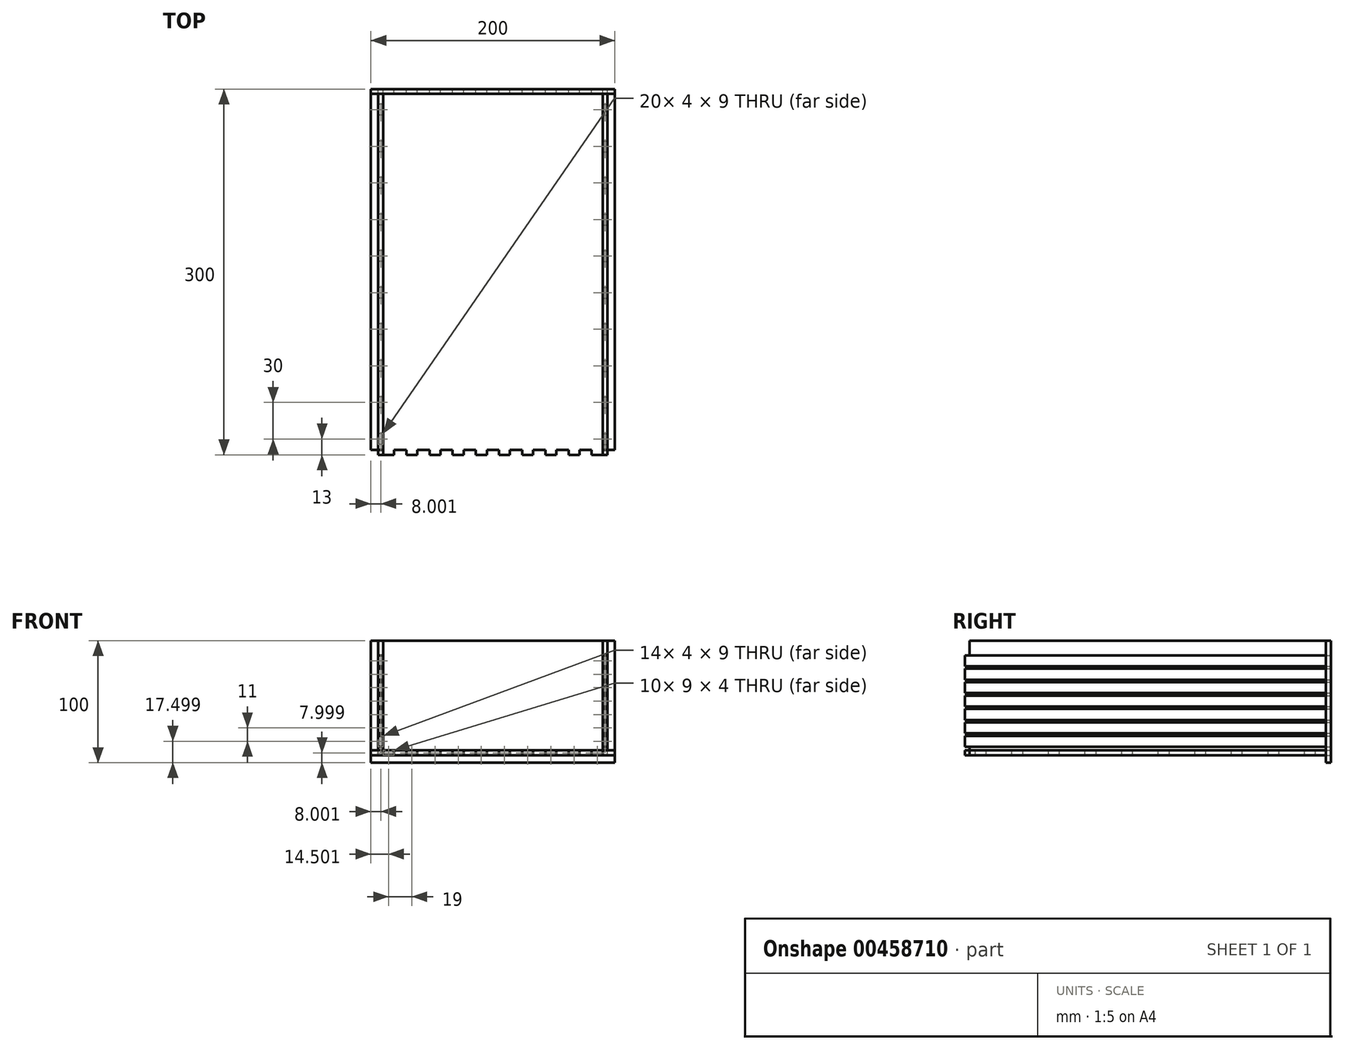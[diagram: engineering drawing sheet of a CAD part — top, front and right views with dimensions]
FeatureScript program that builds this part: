
annotation { "Feature Type Name" : "Feature", "Feature Type Description" : "" }
export const myFeature = defineFeature(function(context is Context, id is Id, definition is map)
    precondition{}
    {
        {
            var Q0;
            Q0=qCreatedBy(makeId("Front.planeOp"),FACE);
            var sketch = newSketch(context, id + "F0", { "sketchPlane" : qUnion([Q0])});
            skLineSegment(sketch, "E0.bottom", {"start": v(-98.88, 5.23) * mm, "end": v(101.12, 5.23) * mm});
            skLineSegment(sketch, "E0.top", {"start": v(-98.88, -94.77) * mm, "end": v(101.12, -94.77) * mm});
            skLineSegment(sketch, "E0.left", {"start": v(-98.88, 5.23) * mm, "end": v(-98.88, -94.77) * mm});
            skLineSegment(sketch, "E0.right", {"start": v(101.12, 5.23) * mm, "end": v(101.12, -94.77) * mm});
            skLineSegment(sketch, "E1.0", {"start": v(-88.88, -4.77) * mm, "end": v(91.12, -4.77) * mm, "construction": true});
            skLineSegment(sketch, "E1.2", {"start": v(-88.88, -84.77) * mm, "end": v(91.12, -84.77) * mm, "construction": true});
            skLineSegment(sketch, "E2.bottom", {"start": v(-88.88, -4.77) * mm, "end": v(-79.88, -4.77) * mm});
            skLineSegment(sketch, "E3.direction1", {"start": v(-88.88, -4.77) * mm, "end": v(-69.88, -4.77) * mm, "construction": true});
            skLineSegment(sketch, "E4.0.9.0", {"start": v(82.12, -4.77) * mm, "end": v(91.12, -4.77) * mm});
            skLineSegment(sketch, "E5", {"start": v(-98.88, -44.77) * mm, "end": v(101.12, -44.77) * mm, "construction": true});
            skLineSegment(sketch, "E6.MirrorCS", {"start": v(-88.88, -84.77) * mm, "end": v(-88.88, -88.77) * mm});
            skLineSegment(sketch, "E7.MirrorCS", {"start": v(-79.88, -84.77) * mm, "end": v(-79.88, -88.77) * mm});
            skLineSegment(sketch, "E8.MirrorCS", {"start": v(-88.88, -88.77) * mm, "end": v(-79.88, -88.77) * mm});
            skLineSegment(sketch, "E9.MirrorCS", {"start": v(-88.88, -84.77) * mm, "end": v(-79.88, -84.77) * mm});
            skLineSegment(sketch, "E10.1.0.0", {"start": v(-60.88, -84.77) * mm, "end": v(-60.88, -88.77) * mm});
            skLineSegment(sketch, "E10.1.0.1", {"start": v(-69.88, -88.77) * mm, "end": v(-60.88, -88.77) * mm});
            skLineSegment(sketch, "E10.1.0.2", {"start": v(-69.88, -84.77) * mm, "end": v(-69.88, -88.77) * mm});
            skLineSegment(sketch, "E10.1.0.3", {"start": v(-69.88, -84.77) * mm, "end": v(-60.88, -84.77) * mm});
            skLineSegment(sketch, "E10.2.0.0", {"start": v(-41.88, -84.77) * mm, "end": v(-41.88, -88.77) * mm});
            skLineSegment(sketch, "E10.2.0.1", {"start": v(-50.88, -88.77) * mm, "end": v(-41.88, -88.77) * mm});
            skLineSegment(sketch, "E10.2.0.2", {"start": v(-50.88, -84.77) * mm, "end": v(-50.88, -88.77) * mm});
            skLineSegment(sketch, "E10.2.0.3", {"start": v(-50.88, -84.77) * mm, "end": v(-41.88, -84.77) * mm});
            skLineSegment(sketch, "E10.3.0.0", {"start": v(-22.88, -84.77) * mm, "end": v(-22.88, -88.77) * mm});
            skLineSegment(sketch, "E10.3.0.1", {"start": v(-31.88, -88.77) * mm, "end": v(-22.88, -88.77) * mm});
            skLineSegment(sketch, "E10.3.0.2", {"start": v(-31.88, -84.77) * mm, "end": v(-31.88, -88.77) * mm});
            skLineSegment(sketch, "E10.3.0.3", {"start": v(-31.88, -84.77) * mm, "end": v(-22.88, -84.77) * mm});
            skLineSegment(sketch, "E10.4.0.0", {"start": v(-3.88, -84.77) * mm, "end": v(-3.88, -88.77) * mm});
            skLineSegment(sketch, "E10.4.0.1", {"start": v(-12.88, -88.77) * mm, "end": v(-3.88, -88.77) * mm});
            skLineSegment(sketch, "E10.4.0.2", {"start": v(-12.88, -84.77) * mm, "end": v(-12.88, -88.77) * mm});
            skLineSegment(sketch, "E10.4.0.3", {"start": v(-12.88, -84.77) * mm, "end": v(-3.88, -84.77) * mm});
            skLineSegment(sketch, "E10.5.0.0", {"start": v(15.12, -84.77) * mm, "end": v(15.12, -88.77) * mm});
            skLineSegment(sketch, "E10.5.0.1", {"start": v(6.12, -88.77) * mm, "end": v(15.12, -88.77) * mm});
            skLineSegment(sketch, "E10.5.0.2", {"start": v(6.12, -84.77) * mm, "end": v(6.12, -88.77) * mm});
            skLineSegment(sketch, "E10.5.0.3", {"start": v(6.12, -84.77) * mm, "end": v(15.12, -84.77) * mm});
            skLineSegment(sketch, "E10.6.0.0", {"start": v(34.12, -84.77) * mm, "end": v(34.12, -88.77) * mm});
            skLineSegment(sketch, "E10.6.0.1", {"start": v(25.12, -88.77) * mm, "end": v(34.12, -88.77) * mm});
            skLineSegment(sketch, "E10.6.0.2", {"start": v(25.12, -84.77) * mm, "end": v(25.12, -88.77) * mm});
            skLineSegment(sketch, "E10.6.0.3", {"start": v(25.12, -84.77) * mm, "end": v(34.12, -84.77) * mm});
            skLineSegment(sketch, "E10.7.0.0", {"start": v(53.12, -84.77) * mm, "end": v(53.12, -88.77) * mm});
            skLineSegment(sketch, "E10.7.0.1", {"start": v(44.12, -88.77) * mm, "end": v(53.12, -88.77) * mm});
            skLineSegment(sketch, "E10.7.0.2", {"start": v(44.12, -84.77) * mm, "end": v(44.12, -88.77) * mm});
            skLineSegment(sketch, "E10.7.0.3", {"start": v(44.12, -84.77) * mm, "end": v(53.12, -84.77) * mm});
            skLineSegment(sketch, "E10.8.0.0", {"start": v(72.12, -84.77) * mm, "end": v(72.12, -88.77) * mm});
            skLineSegment(sketch, "E10.8.0.1", {"start": v(63.12, -88.77) * mm, "end": v(72.12, -88.77) * mm});
            skLineSegment(sketch, "E10.8.0.2", {"start": v(63.12, -84.77) * mm, "end": v(63.12, -88.77) * mm});
            skLineSegment(sketch, "E10.8.0.3", {"start": v(63.12, -84.77) * mm, "end": v(72.12, -84.77) * mm});
            skLineSegment(sketch, "E10.9.0.0", {"start": v(91.12, -84.77) * mm, "end": v(91.12, -88.77) * mm});
            skLineSegment(sketch, "E10.9.0.1", {"start": v(82.12, -88.77) * mm, "end": v(91.12, -88.77) * mm});
            skLineSegment(sketch, "E10.9.0.2", {"start": v(82.12, -84.77) * mm, "end": v(82.12, -88.77) * mm});
            skLineSegment(sketch, "E10.9.0.3", {"start": v(82.12, -84.77) * mm, "end": v(91.12, -84.77) * mm});
            skLineSegment(sketch, "E10.direction1", {"start": v(-79.88, -88.77) * mm, "end": v(-60.88, -88.77) * mm, "construction": true});
            skLineSegment(sketch, "E11.bottom", {"start": v(-88.88, -81.77) * mm, "end": v(-92.88, -81.77) * mm});
            skLineSegment(sketch, "E11.top", {"start": v(-88.88, -72.77) * mm, "end": v(-92.88, -72.77) * mm});
            skLineSegment(sketch, "E11.left", {"start": v(-88.88, -81.77) * mm, "end": v(-88.88, -72.77) * mm});
            skLineSegment(sketch, "E11.right", {"start": v(-92.88, -81.77) * mm, "end": v(-92.88, -72.77) * mm});
            skLineSegment(sketch, "E12.0.1.0", {"start": v(-88.88, -61.77) * mm, "end": v(-92.88, -61.77) * mm});
            skLineSegment(sketch, "E12.0.1.1", {"start": v(-92.88, -70.77) * mm, "end": v(-92.88, -61.77) * mm});
            skLineSegment(sketch, "E12.0.1.2", {"start": v(-88.88, -70.77) * mm, "end": v(-92.88, -70.77) * mm});
            skLineSegment(sketch, "E12.0.1.3", {"start": v(-88.88, -70.77) * mm, "end": v(-88.88, -61.77) * mm});
            skLineSegment(sketch, "E12.0.2.0", {"start": v(-88.88, -50.77) * mm, "end": v(-92.88, -50.77) * mm});
            skLineSegment(sketch, "E12.0.2.1", {"start": v(-92.88, -59.77) * mm, "end": v(-92.88, -50.77) * mm});
            skLineSegment(sketch, "E12.0.2.2", {"start": v(-88.88, -59.77) * mm, "end": v(-92.88, -59.77) * mm});
            skLineSegment(sketch, "E12.0.2.3", {"start": v(-88.88, -59.77) * mm, "end": v(-88.88, -50.77) * mm});
            skLineSegment(sketch, "E12.0.3.0", {"start": v(-88.88, -39.77) * mm, "end": v(-92.88, -39.77) * mm});
            skLineSegment(sketch, "E12.0.3.1", {"start": v(-92.88, -48.77) * mm, "end": v(-92.88, -39.77) * mm});
            skLineSegment(sketch, "E12.0.3.2", {"start": v(-88.88, -48.77) * mm, "end": v(-92.88, -48.77) * mm});
            skLineSegment(sketch, "E12.0.3.3", {"start": v(-88.88, -48.77) * mm, "end": v(-88.88, -39.77) * mm});
            skLineSegment(sketch, "E12.0.4.0", {"start": v(-88.88, -28.77) * mm, "end": v(-92.88, -28.77) * mm});
            skLineSegment(sketch, "E12.0.4.1", {"start": v(-92.88, -37.77) * mm, "end": v(-92.88, -28.77) * mm});
            skLineSegment(sketch, "E12.0.4.2", {"start": v(-88.88, -37.77) * mm, "end": v(-92.88, -37.77) * mm});
            skLineSegment(sketch, "E12.0.4.3", {"start": v(-88.88, -37.77) * mm, "end": v(-88.88, -28.77) * mm});
            skLineSegment(sketch, "E12.0.5.0", {"start": v(-88.88, -17.77) * mm, "end": v(-92.88, -17.77) * mm});
            skLineSegment(sketch, "E12.0.5.1", {"start": v(-92.88, -26.77) * mm, "end": v(-92.88, -17.77) * mm});
            skLineSegment(sketch, "E12.0.5.2", {"start": v(-88.88, -26.77) * mm, "end": v(-92.88, -26.77) * mm});
            skLineSegment(sketch, "E12.0.5.3", {"start": v(-88.88, -26.77) * mm, "end": v(-88.88, -17.77) * mm});
            skLineSegment(sketch, "E12.0.6.0", {"start": v(-88.88, -6.77) * mm, "end": v(-92.88, -6.77) * mm});
            skLineSegment(sketch, "E12.0.6.1", {"start": v(-92.88, -15.77) * mm, "end": v(-92.88, -6.77) * mm});
            skLineSegment(sketch, "E12.0.6.2", {"start": v(-88.88, -15.77) * mm, "end": v(-92.88, -15.77) * mm});
            skLineSegment(sketch, "E12.0.6.3", {"start": v(-88.88, -15.77) * mm, "end": v(-88.88, -6.77) * mm});
            skLineSegment(sketch, "E12.direction1", {"start": v(-92.88, -72.77) * mm, "end": v(-67.88, -72.77) * mm, "construction": true});
            skLineSegment(sketch, "E12.direction2", {"start": v(-92.88, -72.77) * mm, "end": v(-92.88, -61.77) * mm, "construction": true});
            skLineSegment(sketch, "E13", {"start": v(1.12, 5.23) * mm, "end": v(1.12, -94.77) * mm, "construction": true});
            skLineSegment(sketch, "E14.MirrorCS", {"start": v(95.12, -81.77) * mm, "end": v(95.12, -72.77) * mm});
            skLineSegment(sketch, "E15.MirrorCS", {"start": v(91.12, -81.77) * mm, "end": v(95.12, -81.77) * mm});
            skLineSegment(sketch, "E16.MirrorCS", {"start": v(91.12, -81.77) * mm, "end": v(91.12, -72.77) * mm});
            skLineSegment(sketch, "E17.MirrorCS", {"start": v(95.12, -72.77) * mm, "end": v(70.12, -72.77) * mm, "construction": true});
            skLineSegment(sketch, "E18.MirrorCS", {"start": v(91.12, -72.77) * mm, "end": v(95.12, -72.77) * mm});
            skLineSegment(sketch, "E19.0.1.0", {"start": v(91.12, -70.77) * mm, "end": v(91.12, -61.77) * mm});
            skLineSegment(sketch, "E19.0.1.1", {"start": v(91.12, -61.77) * mm, "end": v(95.12, -61.77) * mm});
            skLineSegment(sketch, "E19.0.1.2", {"start": v(95.12, -70.77) * mm, "end": v(95.12, -61.77) * mm});
            skLineSegment(sketch, "E19.0.1.3", {"start": v(91.12, -70.77) * mm, "end": v(95.12, -70.77) * mm});
            skLineSegment(sketch, "E19.0.2.0", {"start": v(91.12, -59.77) * mm, "end": v(91.12, -50.77) * mm});
            skLineSegment(sketch, "E19.0.2.1", {"start": v(91.12, -50.77) * mm, "end": v(95.12, -50.77) * mm});
            skLineSegment(sketch, "E19.0.2.2", {"start": v(95.12, -59.77) * mm, "end": v(95.12, -50.77) * mm});
            skLineSegment(sketch, "E19.0.2.3", {"start": v(91.12, -59.77) * mm, "end": v(95.12, -59.77) * mm});
            skLineSegment(sketch, "E19.0.3.0", {"start": v(91.12, -48.77) * mm, "end": v(91.12, -39.77) * mm});
            skLineSegment(sketch, "E19.0.3.1", {"start": v(91.12, -39.77) * mm, "end": v(95.12, -39.77) * mm});
            skLineSegment(sketch, "E19.0.3.2", {"start": v(95.12, -48.77) * mm, "end": v(95.12, -39.77) * mm});
            skLineSegment(sketch, "E19.0.3.3", {"start": v(91.12, -48.77) * mm, "end": v(95.12, -48.77) * mm});
            skLineSegment(sketch, "E19.0.4.0", {"start": v(91.12, -37.77) * mm, "end": v(91.12, -28.77) * mm});
            skLineSegment(sketch, "E19.0.4.1", {"start": v(91.12, -28.77) * mm, "end": v(95.12, -28.77) * mm});
            skLineSegment(sketch, "E19.0.4.2", {"start": v(95.12, -37.77) * mm, "end": v(95.12, -28.77) * mm});
            skLineSegment(sketch, "E19.0.4.3", {"start": v(91.12, -37.77) * mm, "end": v(95.12, -37.77) * mm});
            skLineSegment(sketch, "E19.0.5.0", {"start": v(91.12, -26.77) * mm, "end": v(91.12, -17.77) * mm});
            skLineSegment(sketch, "E19.0.5.1", {"start": v(91.12, -17.77) * mm, "end": v(95.12, -17.77) * mm});
            skLineSegment(sketch, "E19.0.5.2", {"start": v(95.12, -26.77) * mm, "end": v(95.12, -17.77) * mm});
            skLineSegment(sketch, "E19.0.5.3", {"start": v(91.12, -26.77) * mm, "end": v(95.12, -26.77) * mm});
            skLineSegment(sketch, "E19.0.6.0", {"start": v(91.12, -15.77) * mm, "end": v(91.12, -6.77) * mm});
            skLineSegment(sketch, "E19.0.6.1", {"start": v(91.12, -6.77) * mm, "end": v(95.12, -6.77) * mm});
            skLineSegment(sketch, "E19.0.6.2", {"start": v(95.12, -15.77) * mm, "end": v(95.12, -6.77) * mm});
            skLineSegment(sketch, "E19.0.6.3", {"start": v(91.12, -15.77) * mm, "end": v(95.12, -15.77) * mm});
            skLineSegment(sketch, "E19.direction1", {"start": v(91.12, -81.77) * mm, "end": v(116.12, -81.77) * mm, "construction": true});
            skLineSegment(sketch, "E19.direction2", {"start": v(91.12, -81.77) * mm, "end": v(91.12, -70.77) * mm, "construction": true});
            skLineSegment(sketch, "E20", {"start": v(-84.38, -84.77) * mm, "end": v(-84.38, 5.23) * mm, "construction": true});
            skLineSegment(sketch, "E21.MirrorCS", {"start": v(86.62, -84.77) * mm, "end": v(86.62, 5.23) * mm, "construction": true});
            skSolve(sketch);
        }
        {
            var Q0;
            Q0=makeQuery(id+"F0.imprint","IMPRINT",FACE,{"disambiguationData":[TD([[makeQuery(id+"F0.imprint","IMPRINT",EDGE,{"derivedFrom":sQuery(id+"F0.wireOp",EDGE,"E0.bottom")}),-1.0]])]});
            extrude(context, id + "F1", {"entities" : qUnion([Q0]), "depth" : 4 * mm});
        }
        {
            var Q0;
            Q0=makeQuery(id+"F0.imprint","IMPRINT",FACE,{"disambiguationData":[TD([[makeQuery(id+"F0.imprint","IMPRINT",EDGE,{"derivedFrom":sQuery(id+"F0.wireOp",EDGE,"E10.8.0.0")}),-1.0]])]});
            var Q1;
            Q1=makeQuery(id+"F0.imprint","IMPRINT",FACE,{"disambiguationData":[TD([[makeQuery(id+"F0.imprint","IMPRINT",EDGE,{"derivedFrom":sQuery(id+"F0.wireOp",EDGE,"E10.7.0.0")}),-1.0]])]});
            var Q2;
            Q2=makeQuery(id+"F0.imprint","IMPRINT",FACE,{"disambiguationData":[TD([[makeQuery(id+"F0.imprint","IMPRINT",EDGE,{"derivedFrom":sQuery(id+"F0.wireOp",EDGE,"E10.9.0.0")}),-1.0]])]});
            var Q3;
            Q3=makeQuery(id+"F0.imprint","IMPRINT",FACE,{"disambiguationData":[TD([[makeQuery(id+"F0.imprint","IMPRINT",EDGE,{"derivedFrom":sQuery(id+"F0.wireOp",EDGE,"E10.6.0.0")}),-1.0]])]});
            var Q4;
            Q4=makeQuery(id+"F0.imprint","IMPRINT",FACE,{"disambiguationData":[TD([[makeQuery(id+"F0.imprint","IMPRINT",EDGE,{"derivedFrom":sQuery(id+"F0.wireOp",EDGE,"E10.5.0.0")}),-1.0]])]});
            var Q5;
            Q5=makeQuery(id+"F0.imprint","IMPRINT",FACE,{"disambiguationData":[TD([[makeQuery(id+"F0.imprint","IMPRINT",EDGE,{"derivedFrom":sQuery(id+"F0.wireOp",EDGE,"E10.4.0.0")}),-1.0]])]});
            var Q6;
            Q6=makeQuery(id+"F0.imprint","IMPRINT",FACE,{"disambiguationData":[TD([[makeQuery(id+"F0.imprint","IMPRINT",EDGE,{"derivedFrom":sQuery(id+"F0.wireOp",EDGE,"E10.3.0.0")}),-1.0]])]});
            var Q7;
            Q7=makeQuery(id+"F0.imprint","IMPRINT",FACE,{"disambiguationData":[TD([[makeQuery(id+"F0.imprint","IMPRINT",EDGE,{"derivedFrom":sQuery(id+"F0.wireOp",EDGE,"E10.2.0.0")}),-1.0]])]});
            var Q8;
            Q8=makeQuery(id+"F0.imprint","IMPRINT",FACE,{"disambiguationData":[TD([[makeQuery(id+"F0.imprint","IMPRINT",EDGE,{"derivedFrom":sQuery(id+"F0.wireOp",EDGE,"E10.1.0.0")}),-1.0]])]});
            var Q9;
            Q9=makeQuery(id+"F0.imprint","IMPRINT",FACE,{"disambiguationData":[TD([[makeQuery(id+"F0.imprint","IMPRINT",EDGE,{"derivedFrom":sQuery(id+"F0.wireOp",EDGE,"E6.MirrorCS")}),1.0]])]});
            extrude(context, id + "F2", {"entities" : qUnion([Q0, Q1, Q2, Q3, Q4, Q5, Q6, Q7, Q8, Q9]), "depth" : 300 * mm});
        }
        {
            var Q0;
            Q0=makeQuery(id+"F1.opExtrude","CAP_FACE",FACE,{"disambiguationData":[OSD([sQuery(id+"F0.wireOp",EDGE,"E0.bottom"),sQuery(id+"F0.wireOp",EDGE,"E0.top"),sQuery(id+"F0.wireOp",EDGE,"E0.left"),sQuery(id+"F0.wireOp",EDGE,"E0.right"),sQuery(id+"F0.wireOp",EDGE,"E6.MirrorCS"),sQuery(id+"F0.wireOp",EDGE,"E7.MirrorCS"),sQuery(id+"F0.wireOp",EDGE,"E8.MirrorCS"),sQuery(id+"F0.wireOp",EDGE,"E9.MirrorCS"),sQuery(id+"F0.wireOp",EDGE,"E10.1.0.0"),sQuery(id+"F0.wireOp",EDGE,"E10.1.0.1"),sQuery(id+"F0.wireOp",EDGE,"E10.1.0.2"),sQuery(id+"F0.wireOp",EDGE,"E10.1.0.3"),sQuery(id+"F0.wireOp",EDGE,"E10.2.0.0"),sQuery(id+"F0.wireOp",EDGE,"E10.2.0.1"),sQuery(id+"F0.wireOp",EDGE,"E10.2.0.2"),sQuery(id+"F0.wireOp",EDGE,"E10.2.0.3"),sQuery(id+"F0.wireOp",EDGE,"E10.3.0.0"),sQuery(id+"F0.wireOp",EDGE,"E10.3.0.1"),sQuery(id+"F0.wireOp",EDGE,"E10.3.0.2"),sQuery(id+"F0.wireOp",EDGE,"E10.3.0.3"),sQuery(id+"F0.wireOp",EDGE,"E10.4.0.0"),sQuery(id+"F0.wireOp",EDGE,"E10.4.0.1"),sQuery(id+"F0.wireOp",EDGE,"E10.4.0.2"),sQuery(id+"F0.wireOp",EDGE,"E10.4.0.3"),sQuery(id+"F0.wireOp",EDGE,"E10.5.0.0"),sQuery(id+"F0.wireOp",EDGE,"E10.5.0.1"),sQuery(id+"F0.wireOp",EDGE,"E10.5.0.2"),sQuery(id+"F0.wireOp",EDGE,"E10.5.0.3"),sQuery(id+"F0.wireOp",EDGE,"E10.6.0.0"),sQuery(id+"F0.wireOp",EDGE,"E10.6.0.1"),sQuery(id+"F0.wireOp",EDGE,"E10.6.0.2"),sQuery(id+"F0.wireOp",EDGE,"E10.6.0.3"),sQuery(id+"F0.wireOp",EDGE,"E10.7.0.0"),sQuery(id+"F0.wireOp",EDGE,"E10.7.0.1"),sQuery(id+"F0.wireOp",EDGE,"E10.7.0.2"),sQuery(id+"F0.wireOp",EDGE,"E10.7.0.3"),sQuery(id+"F0.wireOp",EDGE,"E10.8.0.0"),sQuery(id+"F0.wireOp",EDGE,"E10.8.0.1"),sQuery(id+"F0.wireOp",EDGE,"E10.8.0.2"),sQuery(id+"F0.wireOp",EDGE,"E10.8.0.3"),sQuery(id+"F0.wireOp",EDGE,"E10.9.0.0"),sQuery(id+"F0.wireOp",EDGE,"E10.9.0.1"),sQuery(id+"F0.wireOp",EDGE,"E10.9.0.2"),sQuery(id+"F0.wireOp",EDGE,"E10.9.0.3"),sQuery(id+"F0.wireOp",EDGE,"E11.bottom"),sQuery(id+"F0.wireOp",EDGE,"E11.top"),sQuery(id+"F0.wireOp",EDGE,"E11.left"),sQuery(id+"F0.wireOp",EDGE,"E11.right"),sQuery(id+"F0.wireOp",EDGE,"E12.0.1.0"),sQuery(id+"F0.wireOp",EDGE,"E12.0.1.1"),sQuery(id+"F0.wireOp",EDGE,"E12.0.1.2"),sQuery(id+"F0.wireOp",EDGE,"E12.0.1.3"),sQuery(id+"F0.wireOp",EDGE,"E12.0.2.0"),sQuery(id+"F0.wireOp",EDGE,"E12.0.2.1"),sQuery(id+"F0.wireOp",EDGE,"E12.0.2.2"),sQuery(id+"F0.wireOp",EDGE,"E12.0.2.3"),sQuery(id+"F0.wireOp",EDGE,"E12.0.3.0"),sQuery(id+"F0.wireOp",EDGE,"E12.0.3.1"),sQuery(id+"F0.wireOp",EDGE,"E12.0.3.2"),sQuery(id+"F0.wireOp",EDGE,"E12.0.3.3"),sQuery(id+"F0.wireOp",EDGE,"E12.0.4.0"),sQuery(id+"F0.wireOp",EDGE,"E12.0.4.1"),sQuery(id+"F0.wireOp",EDGE,"E12.0.4.2"),sQuery(id+"F0.wireOp",EDGE,"E12.0.4.3"),sQuery(id+"F0.wireOp",EDGE,"E12.0.5.0"),sQuery(id+"F0.wireOp",EDGE,"E12.0.5.1"),sQuery(id+"F0.wireOp",EDGE,"E12.0.5.2"),sQuery(id+"F0.wireOp",EDGE,"E12.0.5.3"),sQuery(id+"F0.wireOp",EDGE,"E12.0.6.0"),sQuery(id+"F0.wireOp",EDGE,"E12.0.6.1"),sQuery(id+"F0.wireOp",EDGE,"E12.0.6.2"),sQuery(id+"F0.wireOp",EDGE,"E12.0.6.3"),sQuery(id+"F0.wireOp",EDGE,"E14.MirrorCS"),sQuery(id+"F0.wireOp",EDGE,"E15.MirrorCS"),sQuery(id+"F0.wireOp",EDGE,"E16.MirrorCS"),sQuery(id+"F0.wireOp",EDGE,"E18.MirrorCS"),sQuery(id+"F0.wireOp",EDGE,"E19.0.1.0"),sQuery(id+"F0.wireOp",EDGE,"E19.0.1.1"),sQuery(id+"F0.wireOp",EDGE,"E19.0.1.2"),sQuery(id+"F0.wireOp",EDGE,"E19.0.1.3"),sQuery(id+"F0.wireOp",EDGE,"E19.0.2.0"),sQuery(id+"F0.wireOp",EDGE,"E19.0.2.1"),sQuery(id+"F0.wireOp",EDGE,"E19.0.2.2"),sQuery(id+"F0.wireOp",EDGE,"E19.0.2.3"),sQuery(id+"F0.wireOp",EDGE,"E19.0.3.0"),sQuery(id+"F0.wireOp",EDGE,"E19.0.3.1"),sQuery(id+"F0.wireOp",EDGE,"E19.0.3.2"),sQuery(id+"F0.wireOp",EDGE,"E19.0.3.3"),sQuery(id+"F0.wireOp",EDGE,"E19.0.4.0"),sQuery(id+"F0.wireOp",EDGE,"E19.0.4.1"),sQuery(id+"F0.wireOp",EDGE,"E19.0.4.2"),sQuery(id+"F0.wireOp",EDGE,"E19.0.4.3"),sQuery(id+"F0.wireOp",EDGE,"E19.0.5.0"),sQuery(id+"F0.wireOp",EDGE,"E19.0.5.1"),sQuery(id+"F0.wireOp",EDGE,"E19.0.5.2"),sQuery(id+"F0.wireOp",EDGE,"E19.0.5.3"),sQuery(id+"F0.wireOp",EDGE,"E19.0.6.0"),sQuery(id+"F0.wireOp",EDGE,"E19.0.6.1"),sQuery(id+"F0.wireOp",EDGE,"E19.0.6.2"),sQuery(id+"F0.wireOp",EDGE,"E19.0.6.3")])],"isStart":false});
            var sketch = newSketch(context, id + "F3", { "sketchPlane" : qUnion([Q0])});
            skLineSegment(sketch, "E22.bottom", {"start": v(-79.88, -84.77) * mm, "end": v(-69.88, -84.77) * mm});
            skLineSegment(sketch, "E22.top", {"start": v(-79.88, -88.77) * mm, "end": v(-69.88, -88.77) * mm});
            skLineSegment(sketch, "E22.left", {"start": v(-79.88, -84.77) * mm, "end": v(-79.88, -88.77) * mm});
            skLineSegment(sketch, "E22.right", {"start": v(-69.88, -84.77) * mm, "end": v(-69.88, -88.77) * mm});
            skLineSegment(sketch, "E23.1.0.0", {"start": v(-60.88, -84.77) * mm, "end": v(-50.88, -84.77) * mm});
            skLineSegment(sketch, "E23.1.0.1", {"start": v(-60.88, -84.77) * mm, "end": v(-60.88, -88.77) * mm});
            skLineSegment(sketch, "E23.1.0.2", {"start": v(-60.88, -88.77) * mm, "end": v(-50.88, -88.77) * mm});
            skLineSegment(sketch, "E23.1.0.3", {"start": v(-50.88, -84.77) * mm, "end": v(-50.88, -88.77) * mm});
            skLineSegment(sketch, "E23.2.0.0", {"start": v(-41.88, -84.77) * mm, "end": v(-31.88, -84.77) * mm});
            skLineSegment(sketch, "E23.2.0.1", {"start": v(-41.88, -84.77) * mm, "end": v(-41.88, -88.77) * mm});
            skLineSegment(sketch, "E23.2.0.2", {"start": v(-41.88, -88.77) * mm, "end": v(-31.88, -88.77) * mm});
            skLineSegment(sketch, "E23.2.0.3", {"start": v(-31.88, -84.77) * mm, "end": v(-31.88, -88.77) * mm});
            skLineSegment(sketch, "E23.3.0.0", {"start": v(-22.88, -84.77) * mm, "end": v(-12.88, -84.77) * mm});
            skLineSegment(sketch, "E23.3.0.1", {"start": v(-22.88, -84.77) * mm, "end": v(-22.88, -88.77) * mm});
            skLineSegment(sketch, "E23.3.0.2", {"start": v(-22.88, -88.77) * mm, "end": v(-12.88, -88.77) * mm});
            skLineSegment(sketch, "E23.3.0.3", {"start": v(-12.88, -84.77) * mm, "end": v(-12.88, -88.77) * mm});
            skLineSegment(sketch, "E23.4.0.0", {"start": v(-3.88, -84.77) * mm, "end": v(6.12, -84.77) * mm});
            skLineSegment(sketch, "E23.4.0.1", {"start": v(-3.88, -84.77) * mm, "end": v(-3.88, -88.77) * mm});
            skLineSegment(sketch, "E23.4.0.2", {"start": v(-3.88, -88.77) * mm, "end": v(6.12, -88.77) * mm});
            skLineSegment(sketch, "E23.4.0.3", {"start": v(6.12, -84.77) * mm, "end": v(6.12, -88.77) * mm});
            skLineSegment(sketch, "E23.5.0.0", {"start": v(15.12, -84.77) * mm, "end": v(25.12, -84.77) * mm});
            skLineSegment(sketch, "E23.5.0.1", {"start": v(15.12, -84.77) * mm, "end": v(15.12, -88.77) * mm});
            skLineSegment(sketch, "E23.5.0.2", {"start": v(15.12, -88.77) * mm, "end": v(25.12, -88.77) * mm});
            skLineSegment(sketch, "E23.5.0.3", {"start": v(25.12, -84.77) * mm, "end": v(25.12, -88.77) * mm});
            skLineSegment(sketch, "E23.6.0.0", {"start": v(34.12, -84.77) * mm, "end": v(44.12, -84.77) * mm});
            skLineSegment(sketch, "E23.6.0.1", {"start": v(34.12, -84.77) * mm, "end": v(34.12, -88.77) * mm});
            skLineSegment(sketch, "E23.6.0.2", {"start": v(34.12, -88.77) * mm, "end": v(44.12, -88.77) * mm});
            skLineSegment(sketch, "E23.6.0.3", {"start": v(44.12, -84.77) * mm, "end": v(44.12, -88.77) * mm});
            skLineSegment(sketch, "E23.7.0.0", {"start": v(53.12, -84.77) * mm, "end": v(63.12, -84.77) * mm});
            skLineSegment(sketch, "E23.7.0.1", {"start": v(53.12, -84.77) * mm, "end": v(53.12, -88.77) * mm});
            skLineSegment(sketch, "E23.7.0.2", {"start": v(53.12, -88.77) * mm, "end": v(63.12, -88.77) * mm});
            skLineSegment(sketch, "E23.7.0.3", {"start": v(63.12, -84.77) * mm, "end": v(63.12, -88.77) * mm});
            skLineSegment(sketch, "E23.8.0.0", {"start": v(72.12, -84.77) * mm, "end": v(82.12, -84.77) * mm});
            skLineSegment(sketch, "E23.8.0.1", {"start": v(72.12, -84.77) * mm, "end": v(72.12, -88.77) * mm});
            skLineSegment(sketch, "E23.8.0.2", {"start": v(72.12, -88.77) * mm, "end": v(82.12, -88.77) * mm});
            skLineSegment(sketch, "E23.8.0.3", {"start": v(82.12, -84.77) * mm, "end": v(82.12, -88.77) * mm});
            skLineSegment(sketch, "E23.direction1", {"start": v(-79.88, -84.77) * mm, "end": v(-60.88, -84.77) * mm, "construction": true});
            skSolve(sketch);
        }
        {
            var Q0;
            Q0=makeQuery(id+"F3.imprint","IMPRINT",FACE,{"disambiguationData":[TD([[makeQuery(id+"F3.imprint","IMPRINT",EDGE,{"derivedFrom":sQuery(id+"F3.wireOp",EDGE,"E22.bottom")}),-1.0]])]});
            var Q1;
            Q1=makeQuery(id+"F3.imprint","IMPRINT",FACE,{"disambiguationData":[TD([[makeQuery(id+"F3.imprint","IMPRINT",EDGE,{"derivedFrom":sQuery(id+"F3.wireOp",EDGE,"E23.1.0.0")}),-1.0]])]});
            var Q2;
            Q2=makeQuery(id+"F3.imprint","IMPRINT",FACE,{"disambiguationData":[TD([[makeQuery(id+"F3.imprint","IMPRINT",EDGE,{"derivedFrom":sQuery(id+"F3.wireOp",EDGE,"E23.2.0.0")}),-1.0]])]});
            var Q3;
            Q3=makeQuery(id+"F3.imprint","IMPRINT",FACE,{"disambiguationData":[TD([[makeQuery(id+"F3.imprint","IMPRINT",EDGE,{"derivedFrom":sQuery(id+"F3.wireOp",EDGE,"E23.3.0.0")}),-1.0]])]});
            var Q4;
            Q4=makeQuery(id+"F3.imprint","IMPRINT",FACE,{"disambiguationData":[TD([[makeQuery(id+"F3.imprint","IMPRINT",EDGE,{"derivedFrom":sQuery(id+"F3.wireOp",EDGE,"E23.4.0.0")}),-1.0]])]});
            var Q5;
            Q5=makeQuery(id+"F3.imprint","IMPRINT",FACE,{"disambiguationData":[TD([[makeQuery(id+"F3.imprint","IMPRINT",EDGE,{"derivedFrom":sQuery(id+"F3.wireOp",EDGE,"E23.6.0.0")}),-1.0]])]});
            var Q6;
            Q6=makeQuery(id+"F3.imprint","IMPRINT",FACE,{"disambiguationData":[TD([[makeQuery(id+"F3.imprint","IMPRINT",EDGE,{"derivedFrom":sQuery(id+"F3.wireOp",EDGE,"E23.7.0.0")}),-1.0]])]});
            var Q7;
            Q7=makeQuery(id+"F3.imprint","IMPRINT",FACE,{"disambiguationData":[TD([[makeQuery(id+"F3.imprint","IMPRINT",EDGE,{"derivedFrom":sQuery(id+"F3.wireOp",EDGE,"E23.8.0.0")}),-1.0]])]});
            var Q8;
            Q8=makeQuery(id+"F3.imprint","IMPRINT",FACE,{"disambiguationData":[TD([[makeQuery(id+"F3.imprint","IMPRINT",EDGE,{"derivedFrom":sQuery(id+"F3.wireOp",EDGE,"E23.5.0.0")}),-1.0]])]});
            extrude(context, id + "F4", {"entities" : qUnion([Q0, Q1, Q2, Q3, Q4, Q5, Q6, Q7, Q8]), "depth" : 292 * mm});
        }
        {
            var Q0;
            Q0=makeQuery(id+"F2.opExtrude","SWEPT_BODY",BODY,{"disambiguationData":[OSD([sQuery(id+"F0.wireOp",EDGE,"E6.MirrorCS"),sQuery(id+"F0.wireOp",EDGE,"E7.MirrorCS"),sQuery(id+"F0.wireOp",EDGE,"E8.MirrorCS"),sQuery(id+"F0.wireOp",EDGE,"E9.MirrorCS")])]});
            var Q1;
            Q1=makeQuery(id+"F2.opExtrude","SWEPT_BODY",BODY,{"disambiguationData":[OSD([sQuery(id+"F0.wireOp",EDGE,"E10.1.0.0"),sQuery(id+"F0.wireOp",EDGE,"E10.1.0.1"),sQuery(id+"F0.wireOp",EDGE,"E10.1.0.2"),sQuery(id+"F0.wireOp",EDGE,"E10.1.0.3")])]});
            var Q2;
            Q2=makeQuery(id+"F2.opExtrude","SWEPT_BODY",BODY,{"disambiguationData":[OSD([sQuery(id+"F0.wireOp",EDGE,"E10.2.0.0"),sQuery(id+"F0.wireOp",EDGE,"E10.2.0.1"),sQuery(id+"F0.wireOp",EDGE,"E10.2.0.2"),sQuery(id+"F0.wireOp",EDGE,"E10.2.0.3")])]});
            var Q3;
            Q3=makeQuery(id+"F2.opExtrude","SWEPT_BODY",BODY,{"disambiguationData":[OSD([sQuery(id+"F0.wireOp",EDGE,"E10.3.0.0"),sQuery(id+"F0.wireOp",EDGE,"E10.3.0.1"),sQuery(id+"F0.wireOp",EDGE,"E10.3.0.2"),sQuery(id+"F0.wireOp",EDGE,"E10.3.0.3")])]});
            var Q4;
            Q4=makeQuery(id+"F2.opExtrude","SWEPT_BODY",BODY,{"disambiguationData":[OSD([sQuery(id+"F0.wireOp",EDGE,"E10.4.0.0"),sQuery(id+"F0.wireOp",EDGE,"E10.4.0.1"),sQuery(id+"F0.wireOp",EDGE,"E10.4.0.2"),sQuery(id+"F0.wireOp",EDGE,"E10.4.0.3")])]});
            var Q5;
            Q5=makeQuery(id+"F2.opExtrude","SWEPT_BODY",BODY,{"disambiguationData":[OSD([sQuery(id+"F0.wireOp",EDGE,"E10.5.0.0"),sQuery(id+"F0.wireOp",EDGE,"E10.5.0.1"),sQuery(id+"F0.wireOp",EDGE,"E10.5.0.2"),sQuery(id+"F0.wireOp",EDGE,"E10.5.0.3")])]});
            var Q6;
            Q6=makeQuery(id+"F2.opExtrude","SWEPT_BODY",BODY,{"disambiguationData":[OSD([sQuery(id+"F0.wireOp",EDGE,"E10.6.0.0"),sQuery(id+"F0.wireOp",EDGE,"E10.6.0.1"),sQuery(id+"F0.wireOp",EDGE,"E10.6.0.2"),sQuery(id+"F0.wireOp",EDGE,"E10.6.0.3")])]});
            var Q7;
            Q7=makeQuery(id+"F2.opExtrude","SWEPT_BODY",BODY,{"disambiguationData":[OSD([sQuery(id+"F0.wireOp",EDGE,"E10.7.0.0"),sQuery(id+"F0.wireOp",EDGE,"E10.7.0.1"),sQuery(id+"F0.wireOp",EDGE,"E10.7.0.2"),sQuery(id+"F0.wireOp",EDGE,"E10.7.0.3")])]});
            var Q8;
            Q8=makeQuery(id+"F2.opExtrude","SWEPT_BODY",BODY,{"disambiguationData":[OSD([sQuery(id+"F0.wireOp",EDGE,"E10.8.0.0"),sQuery(id+"F0.wireOp",EDGE,"E10.8.0.1"),sQuery(id+"F0.wireOp",EDGE,"E10.8.0.2"),sQuery(id+"F0.wireOp",EDGE,"E10.8.0.3")])]});
            var Q9;
            Q9=makeQuery(id+"F2.opExtrude","SWEPT_BODY",BODY,{"disambiguationData":[OSD([sQuery(id+"F0.wireOp",EDGE,"E10.9.0.0"),sQuery(id+"F0.wireOp",EDGE,"E10.9.0.1"),sQuery(id+"F0.wireOp",EDGE,"E10.9.0.2"),sQuery(id+"F0.wireOp",EDGE,"E10.9.0.3")])]});
            var Q10;
            Q10=makeQuery(id+"F4.opExtrude","SWEPT_BODY",BODY,{"disambiguationData":[OSD([sQuery(id+"F3.wireOp",EDGE,"E22.bottom"),sQuery(id+"F3.wireOp",EDGE,"E22.top"),sQuery(id+"F3.wireOp",EDGE,"E22.left"),sQuery(id+"F3.wireOp",EDGE,"E22.right")])]});
            var Q11;
            Q11=makeQuery(id+"F4.opExtrude","SWEPT_BODY",BODY,{"disambiguationData":[OSD([sQuery(id+"F3.wireOp",EDGE,"E23.1.0.0"),sQuery(id+"F3.wireOp",EDGE,"E23.1.0.1"),sQuery(id+"F3.wireOp",EDGE,"E23.1.0.2"),sQuery(id+"F3.wireOp",EDGE,"E23.1.0.3")])]});
            var Q12;
            Q12=makeQuery(id+"F4.opExtrude","SWEPT_BODY",BODY,{"disambiguationData":[OSD([sQuery(id+"F3.wireOp",EDGE,"E23.4.0.0"),sQuery(id+"F3.wireOp",EDGE,"E23.4.0.1"),sQuery(id+"F3.wireOp",EDGE,"E23.4.0.2"),sQuery(id+"F3.wireOp",EDGE,"E23.4.0.3")])]});
            var Q13;
            Q13=makeQuery(id+"F4.opExtrude","SWEPT_BODY",BODY,{"disambiguationData":[OSD([sQuery(id+"F3.wireOp",EDGE,"E23.5.0.0"),sQuery(id+"F3.wireOp",EDGE,"E23.5.0.1"),sQuery(id+"F3.wireOp",EDGE,"E23.5.0.2"),sQuery(id+"F3.wireOp",EDGE,"E23.5.0.3")])]});
            var Q14;
            Q14=makeQuery(id+"F4.opExtrude","SWEPT_BODY",BODY,{"disambiguationData":[OSD([sQuery(id+"F3.wireOp",EDGE,"E23.3.0.0"),sQuery(id+"F3.wireOp",EDGE,"E23.3.0.1"),sQuery(id+"F3.wireOp",EDGE,"E23.3.0.2"),sQuery(id+"F3.wireOp",EDGE,"E23.3.0.3")])]});
            var Q15;
            Q15=makeQuery(id+"F4.opExtrude","SWEPT_BODY",BODY,{"disambiguationData":[OSD([sQuery(id+"F3.wireOp",EDGE,"E23.2.0.0"),sQuery(id+"F3.wireOp",EDGE,"E23.2.0.1"),sQuery(id+"F3.wireOp",EDGE,"E23.2.0.2"),sQuery(id+"F3.wireOp",EDGE,"E23.2.0.3")])]});
            var Q16;
            Q16=makeQuery(id+"F4.opExtrude","SWEPT_BODY",BODY,{"disambiguationData":[OSD([sQuery(id+"F3.wireOp",EDGE,"E23.7.0.0"),sQuery(id+"F3.wireOp",EDGE,"E23.7.0.1"),sQuery(id+"F3.wireOp",EDGE,"E23.7.0.2"),sQuery(id+"F3.wireOp",EDGE,"E23.7.0.3")])]});
            var Q17;
            Q17=makeQuery(id+"F4.opExtrude","SWEPT_BODY",BODY,{"disambiguationData":[OSD([sQuery(id+"F3.wireOp",EDGE,"E23.6.0.0"),sQuery(id+"F3.wireOp",EDGE,"E23.6.0.1"),sQuery(id+"F3.wireOp",EDGE,"E23.6.0.2"),sQuery(id+"F3.wireOp",EDGE,"E23.6.0.3")])]});
            var Q18;
            Q18=makeQuery(id+"F4.opExtrude","SWEPT_BODY",BODY,{"disambiguationData":[OSD([sQuery(id+"F3.wireOp",EDGE,"E23.8.0.0"),sQuery(id+"F3.wireOp",EDGE,"E23.8.0.1"),sQuery(id+"F3.wireOp",EDGE,"E23.8.0.2"),sQuery(id+"F3.wireOp",EDGE,"E23.8.0.3")])]});
            booleanBodies(context, id + "F5", {"operationType" : BooleanOperationType.UNION, "tools" : qUnion([Q0, Q1, Q2, Q3, Q4, Q5, Q6, Q7, Q8, Q9, Q10, Q11, Q12, Q13, Q14, Q15, Q16, Q17, Q18])});
        }
        {
            var Q0;
            Q0=makeQuery(id+"F2.opExtrude","SWEPT_FACE",FACE,{"disambiguationData":[OSD([sQuery(id+"F0.wireOp",EDGE,"E6.MirrorCS")])]});
            var sketch = newSketch(context, id + "F6", { "sketchPlane" : qUnion([Q0])});
            skLineSegment(sketch, "E24", {"start": v(4, -84.77) * mm, "end": v(4, -88.77) * mm});
            skLineSegment(sketch, "E25", {"start": v(296, -84.77) * mm, "end": v(296, -88.77) * mm});
            skSolve(sketch);
        }
        {
            var Q0;
            {var subQ0=sQuery(id+"F6.wireOp",EDGE,"E24");Q0=makeQuery(id+"F6.imprint","IMPRINT",FACE,{"disambiguationData":[TD([[makeQuery(id+"F6.imprint","IMPRINT",EDGE,{"derivedFrom":subQ0}),1.0]])]});}
            extrude(context, id + "F7", {"entities" : qUnion([Q0]), "depth" : 10 * mm});
        }
        {
            var Q0;
            Q0=makeQuery(id+"F2.opExtrude","SWEPT_BODY",BODY,{"disambiguationData":[OSD([sQuery(id+"F0.wireOp",EDGE,"E6.MirrorCS"),sQuery(id+"F0.wireOp",EDGE,"E7.MirrorCS"),sQuery(id+"F0.wireOp",EDGE,"E8.MirrorCS"),sQuery(id+"F0.wireOp",EDGE,"E9.MirrorCS")])]});
            var Q1;
            Q1=makeQuery(id+"F7.opExtrude","SWEPT_BODY",BODY,{"disambiguationData":[OSD([sQuery(id+"F0.wireOp",EDGE,"E6.MirrorCS"),sQuery(id+"F0.wireOp",EDGE,"E8.MirrorCS"),sQuery(id+"F0.wireOp",EDGE,"E9.MirrorCS")])]});
            booleanBodies(context, id + "F8", {"operationType" : BooleanOperationType.UNION, "tools" : qUnion([Q0, Q1])});
        }
        {
            var Q0;
            Q0=makeQuery(id+"F2.opExtrude","SWEPT_FACE",FACE,{"disambiguationData":[OSD([sQuery(id+"F0.wireOp",EDGE,"E10.9.0.0")])]});
            var sketch = newSketch(context, id + "F9", { "sketchPlane" : qUnion([Q0])});
            skLineSegment(sketch, "E26", {"start": v(13.3, -84.77) * mm, "end": v(13.3, -87.46) * mm});
            skLineSegment(sketch, "E27", {"start": v(-4, -84.77) * mm, "end": v(-4, -88.77) * mm});
            skLineSegment(sketch, "E28", {"start": v(-296, -84.77) * mm, "end": v(-296, -88.77) * mm});
            skSolve(sketch);
        }
        {
            var Q0;
            {var subQ0=sQuery(id+"F9.wireOp",EDGE,"E27");Q0=makeQuery(id+"F9.imprint","IMPRINT",FACE,{"disambiguationData":[TD([[makeQuery(id+"F9.imprint","IMPRINT",EDGE,{"derivedFrom":subQ0}),-1.0]])]});}
            extrude(context, id + "F10", {"entities" : qUnion([Q0]), "depth" : 10 * mm});
        }
        {
            var Q0;
            Q0=makeQuery(id+"F10.opExtrude","SWEPT_BODY",BODY,{"disambiguationData":[OSD([sQuery(id+"F0.wireOp",EDGE,"E10.9.0.0"),sQuery(id+"F0.wireOp",EDGE,"E10.9.0.1"),sQuery(id+"F0.wireOp",EDGE,"E10.9.0.3")])]});
            var Q1;
            Q1=makeQuery(id+"F2.opExtrude","SWEPT_BODY",BODY,{"disambiguationData":[OSD([sQuery(id+"F0.wireOp",EDGE,"E6.MirrorCS"),sQuery(id+"F0.wireOp",EDGE,"E7.MirrorCS"),sQuery(id+"F0.wireOp",EDGE,"E8.MirrorCS"),sQuery(id+"F0.wireOp",EDGE,"E9.MirrorCS")])]});
            booleanBodies(context, id + "F11", {"operationType" : BooleanOperationType.UNION, "tools" : qUnion([Q0, Q1])});
        }
        {
            var Q0;
            Q0=makeQuery(id+"F1.opExtrude","CAP_FACE",FACE,{"disambiguationData":[OSD([sQuery(id+"F0.wireOp",EDGE,"E0.bottom"),sQuery(id+"F0.wireOp",EDGE,"E0.top"),sQuery(id+"F0.wireOp",EDGE,"E0.left"),sQuery(id+"F0.wireOp",EDGE,"E0.right"),sQuery(id+"F0.wireOp",EDGE,"E6.MirrorCS"),sQuery(id+"F0.wireOp",EDGE,"E7.MirrorCS"),sQuery(id+"F0.wireOp",EDGE,"E8.MirrorCS"),sQuery(id+"F0.wireOp",EDGE,"E9.MirrorCS"),sQuery(id+"F0.wireOp",EDGE,"E10.1.0.0"),sQuery(id+"F0.wireOp",EDGE,"E10.1.0.1"),sQuery(id+"F0.wireOp",EDGE,"E10.1.0.2"),sQuery(id+"F0.wireOp",EDGE,"E10.1.0.3"),sQuery(id+"F0.wireOp",EDGE,"E10.2.0.0"),sQuery(id+"F0.wireOp",EDGE,"E10.2.0.1"),sQuery(id+"F0.wireOp",EDGE,"E10.2.0.2"),sQuery(id+"F0.wireOp",EDGE,"E10.2.0.3"),sQuery(id+"F0.wireOp",EDGE,"E10.3.0.0"),sQuery(id+"F0.wireOp",EDGE,"E10.3.0.1"),sQuery(id+"F0.wireOp",EDGE,"E10.3.0.2"),sQuery(id+"F0.wireOp",EDGE,"E10.3.0.3"),sQuery(id+"F0.wireOp",EDGE,"E10.4.0.0"),sQuery(id+"F0.wireOp",EDGE,"E10.4.0.1"),sQuery(id+"F0.wireOp",EDGE,"E10.4.0.2"),sQuery(id+"F0.wireOp",EDGE,"E10.4.0.3"),sQuery(id+"F0.wireOp",EDGE,"E10.5.0.0"),sQuery(id+"F0.wireOp",EDGE,"E10.5.0.1"),sQuery(id+"F0.wireOp",EDGE,"E10.5.0.2"),sQuery(id+"F0.wireOp",EDGE,"E10.5.0.3"),sQuery(id+"F0.wireOp",EDGE,"E10.6.0.0"),sQuery(id+"F0.wireOp",EDGE,"E10.6.0.1"),sQuery(id+"F0.wireOp",EDGE,"E10.6.0.2"),sQuery(id+"F0.wireOp",EDGE,"E10.6.0.3"),sQuery(id+"F0.wireOp",EDGE,"E10.7.0.0"),sQuery(id+"F0.wireOp",EDGE,"E10.7.0.1"),sQuery(id+"F0.wireOp",EDGE,"E10.7.0.2"),sQuery(id+"F0.wireOp",EDGE,"E10.7.0.3"),sQuery(id+"F0.wireOp",EDGE,"E10.8.0.0"),sQuery(id+"F0.wireOp",EDGE,"E10.8.0.1"),sQuery(id+"F0.wireOp",EDGE,"E10.8.0.2"),sQuery(id+"F0.wireOp",EDGE,"E10.8.0.3"),sQuery(id+"F0.wireOp",EDGE,"E10.9.0.0"),sQuery(id+"F0.wireOp",EDGE,"E10.9.0.1"),sQuery(id+"F0.wireOp",EDGE,"E10.9.0.2"),sQuery(id+"F0.wireOp",EDGE,"E10.9.0.3"),sQuery(id+"F0.wireOp",EDGE,"E11.bottom"),sQuery(id+"F0.wireOp",EDGE,"E11.top"),sQuery(id+"F0.wireOp",EDGE,"E11.left"),sQuery(id+"F0.wireOp",EDGE,"E11.right"),sQuery(id+"F0.wireOp",EDGE,"E12.0.1.0"),sQuery(id+"F0.wireOp",EDGE,"E12.0.1.1"),sQuery(id+"F0.wireOp",EDGE,"E12.0.1.2"),sQuery(id+"F0.wireOp",EDGE,"E12.0.1.3"),sQuery(id+"F0.wireOp",EDGE,"E12.0.2.0"),sQuery(id+"F0.wireOp",EDGE,"E12.0.2.1"),sQuery(id+"F0.wireOp",EDGE,"E12.0.2.2"),sQuery(id+"F0.wireOp",EDGE,"E12.0.2.3"),sQuery(id+"F0.wireOp",EDGE,"E12.0.3.0"),sQuery(id+"F0.wireOp",EDGE,"E12.0.3.1"),sQuery(id+"F0.wireOp",EDGE,"E12.0.3.2"),sQuery(id+"F0.wireOp",EDGE,"E12.0.3.3"),sQuery(id+"F0.wireOp",EDGE,"E12.0.4.0"),sQuery(id+"F0.wireOp",EDGE,"E12.0.4.1"),sQuery(id+"F0.wireOp",EDGE,"E12.0.4.2"),sQuery(id+"F0.wireOp",EDGE,"E12.0.4.3"),sQuery(id+"F0.wireOp",EDGE,"E12.0.5.0"),sQuery(id+"F0.wireOp",EDGE,"E12.0.5.1"),sQuery(id+"F0.wireOp",EDGE,"E12.0.5.2"),sQuery(id+"F0.wireOp",EDGE,"E12.0.5.3"),sQuery(id+"F0.wireOp",EDGE,"E12.0.6.0"),sQuery(id+"F0.wireOp",EDGE,"E12.0.6.1"),sQuery(id+"F0.wireOp",EDGE,"E12.0.6.2"),sQuery(id+"F0.wireOp",EDGE,"E12.0.6.3"),sQuery(id+"F0.wireOp",EDGE,"E14.MirrorCS"),sQuery(id+"F0.wireOp",EDGE,"E15.MirrorCS"),sQuery(id+"F0.wireOp",EDGE,"E16.MirrorCS"),sQuery(id+"F0.wireOp",EDGE,"E18.MirrorCS"),sQuery(id+"F0.wireOp",EDGE,"E19.0.1.0"),sQuery(id+"F0.wireOp",EDGE,"E19.0.1.1"),sQuery(id+"F0.wireOp",EDGE,"E19.0.1.2"),sQuery(id+"F0.wireOp",EDGE,"E19.0.1.3"),sQuery(id+"F0.wireOp",EDGE,"E19.0.2.0"),sQuery(id+"F0.wireOp",EDGE,"E19.0.2.1"),sQuery(id+"F0.wireOp",EDGE,"E19.0.2.2"),sQuery(id+"F0.wireOp",EDGE,"E19.0.2.3"),sQuery(id+"F0.wireOp",EDGE,"E19.0.3.0"),sQuery(id+"F0.wireOp",EDGE,"E19.0.3.1"),sQuery(id+"F0.wireOp",EDGE,"E19.0.3.2"),sQuery(id+"F0.wireOp",EDGE,"E19.0.3.3"),sQuery(id+"F0.wireOp",EDGE,"E19.0.4.0"),sQuery(id+"F0.wireOp",EDGE,"E19.0.4.1"),sQuery(id+"F0.wireOp",EDGE,"E19.0.4.2"),sQuery(id+"F0.wireOp",EDGE,"E19.0.4.3"),sQuery(id+"F0.wireOp",EDGE,"E19.0.5.0"),sQuery(id+"F0.wireOp",EDGE,"E19.0.5.1"),sQuery(id+"F0.wireOp",EDGE,"E19.0.5.2"),sQuery(id+"F0.wireOp",EDGE,"E19.0.5.3"),sQuery(id+"F0.wireOp",EDGE,"E19.0.6.0"),sQuery(id+"F0.wireOp",EDGE,"E19.0.6.1"),sQuery(id+"F0.wireOp",EDGE,"E19.0.6.2"),sQuery(id+"F0.wireOp",EDGE,"E19.0.6.3")])],"isStart":false});
            var sketch = newSketch(context, id + "F12", { "sketchPlane" : qUnion([Q0])});
            skLineSegment(sketch, "E29.bottom", {"start": v(-92.88, 5.23) * mm, "end": v(-88.88, 5.23) * mm});
            skLineSegment(sketch, "E29.top", {"start": v(-92.88, -84.77) * mm, "end": v(-88.88, -84.77) * mm});
            skLineSegment(sketch, "E29.left", {"start": v(-92.88, 5.23) * mm, "end": v(-92.88, -84.77) * mm});
            skLineSegment(sketch, "E29.right", {"start": v(-88.88, 5.23) * mm, "end": v(-88.88, -84.77) * mm});
            skLineSegment(sketch, "E30.MirrorCS", {"start": v(91.12, 5.23) * mm, "end": v(91.12, -84.77) * mm});
            skLineSegment(sketch, "E31.MirrorCS", {"start": v(95.12, 5.23) * mm, "end": v(95.12, -84.77) * mm});
            skLineSegment(sketch, "E32.bottom", {"start": v(-92.88, -6.77) * mm, "end": v(-88.88, -6.77) * mm});
            skLineSegment(sketch, "E32.top", {"start": v(-92.88, -15.77) * mm, "end": v(-88.88, -15.77) * mm});
            skLineSegment(sketch, "E32.left", {"start": v(-92.88, -6.77) * mm, "end": v(-92.88, -15.77) * mm});
            skLineSegment(sketch, "E32.right", {"start": v(-88.88, -6.77) * mm, "end": v(-88.88, -15.77) * mm});
            skLineSegment(sketch, "E33.bottom", {"start": v(95.12, -6.77) * mm, "end": v(91.12, -6.77) * mm});
            skLineSegment(sketch, "E33.top", {"start": v(95.12, -15.77) * mm, "end": v(91.12, -15.77) * mm});
            skLineSegment(sketch, "E33.left", {"start": v(95.12, -6.77) * mm, "end": v(95.12, -15.77) * mm});
            skLineSegment(sketch, "E33.right", {"start": v(91.12, -6.77) * mm, "end": v(91.12, -15.77) * mm});
            skLineSegment(sketch, "E34.0.1.0", {"start": v(-92.88, -17.77) * mm, "end": v(-88.88, -17.77) * mm});
            skLineSegment(sketch, "E34.0.1.1", {"start": v(-92.88, -17.77) * mm, "end": v(-92.88, -26.77) * mm});
            skLineSegment(sketch, "E34.0.1.2", {"start": v(-88.88, -17.77) * mm, "end": v(-88.88, -26.77) * mm});
            skLineSegment(sketch, "E34.0.1.3", {"start": v(-92.88, -26.77) * mm, "end": v(-88.88, -26.77) * mm});
            skLineSegment(sketch, "E34.0.2.0", {"start": v(-92.88, -28.77) * mm, "end": v(-88.88, -28.77) * mm});
            skLineSegment(sketch, "E34.0.2.1", {"start": v(-92.88, -28.77) * mm, "end": v(-92.88, -37.77) * mm});
            skLineSegment(sketch, "E34.0.2.2", {"start": v(-88.88, -28.77) * mm, "end": v(-88.88, -37.77) * mm});
            skLineSegment(sketch, "E34.0.2.3", {"start": v(-92.88, -37.77) * mm, "end": v(-88.88, -37.77) * mm});
            skLineSegment(sketch, "E34.0.3.0", {"start": v(-92.88, -39.77) * mm, "end": v(-88.88, -39.77) * mm});
            skLineSegment(sketch, "E34.0.3.1", {"start": v(-92.88, -39.77) * mm, "end": v(-92.88, -48.77) * mm});
            skLineSegment(sketch, "E34.0.3.2", {"start": v(-88.88, -39.77) * mm, "end": v(-88.88, -48.77) * mm});
            skLineSegment(sketch, "E34.0.3.3", {"start": v(-92.88, -48.77) * mm, "end": v(-88.88, -48.77) * mm});
            skLineSegment(sketch, "E34.0.4.0", {"start": v(-92.88, -50.77) * mm, "end": v(-88.88, -50.77) * mm});
            skLineSegment(sketch, "E34.0.4.1", {"start": v(-92.88, -50.77) * mm, "end": v(-92.88, -59.77) * mm});
            skLineSegment(sketch, "E34.0.4.2", {"start": v(-88.88, -50.77) * mm, "end": v(-88.88, -59.77) * mm});
            skLineSegment(sketch, "E34.0.4.3", {"start": v(-92.88, -59.77) * mm, "end": v(-88.88, -59.77) * mm});
            skLineSegment(sketch, "E34.0.5.0", {"start": v(-92.88, -61.77) * mm, "end": v(-88.88, -61.77) * mm});
            skLineSegment(sketch, "E34.0.5.1", {"start": v(-92.88, -61.77) * mm, "end": v(-92.88, -70.77) * mm});
            skLineSegment(sketch, "E34.0.5.2", {"start": v(-88.88, -61.77) * mm, "end": v(-88.88, -70.77) * mm});
            skLineSegment(sketch, "E34.0.5.3", {"start": v(-92.88, -70.77) * mm, "end": v(-88.88, -70.77) * mm});
            skLineSegment(sketch, "E34.0.6.0", {"start": v(-92.88, -72.77) * mm, "end": v(-88.88, -72.77) * mm});
            skLineSegment(sketch, "E34.0.6.1", {"start": v(-92.88, -72.77) * mm, "end": v(-92.88, -81.77) * mm});
            skLineSegment(sketch, "E34.0.6.2", {"start": v(-88.88, -72.77) * mm, "end": v(-88.88, -81.77) * mm});
            skLineSegment(sketch, "E34.0.6.3", {"start": v(-92.88, -81.77) * mm, "end": v(-88.88, -81.77) * mm});
            skLineSegment(sketch, "E34.direction1", {"start": v(-92.88, -6.77) * mm, "end": v(-67.88, -6.77) * mm, "construction": true});
            skLineSegment(sketch, "E34.direction2", {"start": v(-92.88, -6.77) * mm, "end": v(-92.88, -17.77) * mm, "construction": true});
            skLineSegment(sketch, "E35.MirrorCS", {"start": v(95.12, -17.77) * mm, "end": v(91.12, -17.77) * mm});
            skLineSegment(sketch, "E36.MirrorCS", {"start": v(95.12, -28.77) * mm, "end": v(91.12, -28.77) * mm});
            skLineSegment(sketch, "E37.MirrorCS", {"start": v(95.12, -26.77) * mm, "end": v(91.12, -26.77) * mm});
            skLineSegment(sketch, "E38.MirrorCS", {"start": v(95.12, -37.77) * mm, "end": v(91.12, -37.77) * mm});
            skLineSegment(sketch, "E39.MirrorCS", {"start": v(95.12, -39.77) * mm, "end": v(91.12, -39.77) * mm});
            skLineSegment(sketch, "E40.MirrorCS", {"start": v(95.12, -48.77) * mm, "end": v(91.12, -48.77) * mm});
            skLineSegment(sketch, "E41.MirrorCS", {"start": v(95.12, -50.77) * mm, "end": v(91.12, -50.77) * mm});
            skLineSegment(sketch, "E42.MirrorCS", {"start": v(95.12, -59.77) * mm, "end": v(91.12, -59.77) * mm});
            skLineSegment(sketch, "E43.MirrorCS", {"start": v(95.12, -61.77) * mm, "end": v(91.12, -61.77) * mm});
            skLineSegment(sketch, "E44.MirrorCS", {"start": v(95.12, -70.77) * mm, "end": v(91.12, -70.77) * mm});
            skLineSegment(sketch, "E45.MirrorCS", {"start": v(95.12, -72.77) * mm, "end": v(91.12, -72.77) * mm});
            skLineSegment(sketch, "E46.MirrorCS", {"start": v(95.12, -81.77) * mm, "end": v(91.12, -81.77) * mm});
            skSolve(sketch);
        }
        {
            var Q0;
            {var subQ0=sQuery(id+"F0.wireOp",EDGE,"E10.9.0.3");var subQ1=sQuery(id+"F0.wireOp",EDGE,"E9.MirrorCS");Q0=makeQuery(id+"F11.opBoolean","MERGE",FACE,{"derivedFrom":[makeQuery(id+"F8.opBoolean","MERGE",FACE,{"derivedFrom":[makeQuery(id+"F5.opBoolean","MERGE",FACE,{"derivedFrom":[makeQuery(id+"F2.opExtrude","SWEPT_FACE",FACE,{"disambiguationData":[OSD([subQ1])]}),makeQuery(id+"F2.opExtrude","SWEPT_FACE",FACE,{"disambiguationData":[OSD([sQuery(id+"F0.wireOp",EDGE,"E10.1.0.3")])]}),makeQuery(id+"F2.opExtrude","SWEPT_FACE",FACE,{"disambiguationData":[OSD([sQuery(id+"F0.wireOp",EDGE,"E10.2.0.3")])]}),makeQuery(id+"F2.opExtrude","SWEPT_FACE",FACE,{"disambiguationData":[OSD([sQuery(id+"F0.wireOp",EDGE,"E10.3.0.3")])]}),makeQuery(id+"F2.opExtrude","SWEPT_FACE",FACE,{"disambiguationData":[OSD([sQuery(id+"F0.wireOp",EDGE,"E10.4.0.3")])]}),makeQuery(id+"F2.opExtrude","SWEPT_FACE",FACE,{"disambiguationData":[OSD([sQuery(id+"F0.wireOp",EDGE,"E10.5.0.3")])]}),makeQuery(id+"F2.opExtrude","SWEPT_FACE",FACE,{"disambiguationData":[OSD([sQuery(id+"F0.wireOp",EDGE,"E10.6.0.3")])]}),makeQuery(id+"F2.opExtrude","SWEPT_FACE",FACE,{"disambiguationData":[OSD([sQuery(id+"F0.wireOp",EDGE,"E10.7.0.3")])]}),makeQuery(id+"F2.opExtrude","SWEPT_FACE",FACE,{"disambiguationData":[OSD([sQuery(id+"F0.wireOp",EDGE,"E10.8.0.3")])]}),makeQuery(id+"F2.opExtrude","SWEPT_FACE",FACE,{"disambiguationData":[OSD([subQ0])]}),makeQuery(id+"F4.opExtrude","SWEPT_FACE",FACE,{"disambiguationData":[OSD([sQuery(id+"F3.wireOp",EDGE,"E22.bottom")])]}),makeQuery(id+"F4.opExtrude","SWEPT_FACE",FACE,{"disambiguationData":[OSD([sQuery(id+"F3.wireOp",EDGE,"E23.1.0.0")])]}),makeQuery(id+"F4.opExtrude","SWEPT_FACE",FACE,{"disambiguationData":[OSD([sQuery(id+"F3.wireOp",EDGE,"E23.2.0.0")])]}),makeQuery(id+"F4.opExtrude","SWEPT_FACE",FACE,{"disambiguationData":[OSD([sQuery(id+"F3.wireOp",EDGE,"E23.3.0.0")])]}),makeQuery(id+"F4.opExtrude","SWEPT_FACE",FACE,{"disambiguationData":[OSD([sQuery(id+"F3.wireOp",EDGE,"E23.4.0.0")])]}),makeQuery(id+"F4.opExtrude","SWEPT_FACE",FACE,{"disambiguationData":[OSD([sQuery(id+"F3.wireOp",EDGE,"E23.5.0.0")])]}),makeQuery(id+"F4.opExtrude","SWEPT_FACE",FACE,{"disambiguationData":[OSD([sQuery(id+"F3.wireOp",EDGE,"E23.6.0.0")])]}),makeQuery(id+"F4.opExtrude","SWEPT_FACE",FACE,{"disambiguationData":[OSD([sQuery(id+"F3.wireOp",EDGE,"E23.7.0.0")])]}),makeQuery(id+"F4.opExtrude","SWEPT_FACE",FACE,{"disambiguationData":[OSD([sQuery(id+"F3.wireOp",EDGE,"E23.8.0.0")])]})]}),makeQuery(id+"F7.opExtrude","SWEPT_FACE",FACE,{"disambiguationData":[OSD([sQuery(id+"F0.wireOp",EDGE,"E6.MirrorCS"),subQ1])]})]}),makeQuery(id+"F10.opExtrude","SWEPT_FACE",FACE,{"disambiguationData":[OSD([sQuery(id+"F0.wireOp",EDGE,"E10.9.0.0"),subQ0])]})]});}
            var sketch = newSketch(context, id + "F13", { "sketchPlane" : qUnion([Q0])});
            skLineSegment(sketch, "E47.bottom", {"start": v(-88.88, -12.5) * mm, "end": v(-92.88, -12.5) * mm});
            skLineSegment(sketch, "E47.top", {"start": v(-88.88, -21.5) * mm, "end": v(-92.88, -21.5) * mm});
            skLineSegment(sketch, "E47.left", {"start": v(-88.88, -12.5) * mm, "end": v(-88.88, -21.5) * mm});
            skLineSegment(sketch, "E47.right", {"start": v(-92.88, -12.5) * mm, "end": v(-92.88, -21.5) * mm});
            skLineSegment(sketch, "E48.0.1.0", {"start": v(-88.88, -42.5) * mm, "end": v(-88.88, -51.5) * mm});
            skLineSegment(sketch, "E48.0.1.1", {"start": v(-88.88, -42.5) * mm, "end": v(-92.88, -42.5) * mm});
            skLineSegment(sketch, "E48.0.1.2", {"start": v(-92.88, -42.5) * mm, "end": v(-92.88, -51.5) * mm});
            skLineSegment(sketch, "E48.0.2.0", {"start": v(-88.88, -72.5) * mm, "end": v(-88.88, -81.5) * mm});
            skLineSegment(sketch, "E48.0.2.1", {"start": v(-88.88, -72.5) * mm, "end": v(-92.88, -72.5) * mm});
            skLineSegment(sketch, "E48.0.2.2", {"start": v(-92.88, -72.5) * mm, "end": v(-92.88, -81.5) * mm});
            skLineSegment(sketch, "E48.0.3.0", {"start": v(-88.88, -102.5) * mm, "end": v(-88.88, -111.5) * mm});
            skLineSegment(sketch, "E48.0.3.1", {"start": v(-88.88, -102.5) * mm, "end": v(-92.88, -102.5) * mm});
            skLineSegment(sketch, "E48.0.3.2", {"start": v(-92.88, -102.5) * mm, "end": v(-92.88, -111.5) * mm});
            skLineSegment(sketch, "E48.0.4.0", {"start": v(-88.88, -132.5) * mm, "end": v(-88.88, -141.5) * mm});
            skLineSegment(sketch, "E48.0.4.1", {"start": v(-88.88, -132.5) * mm, "end": v(-92.88, -132.5) * mm});
            skLineSegment(sketch, "E48.0.4.2", {"start": v(-92.88, -132.5) * mm, "end": v(-92.88, -141.5) * mm});
            skLineSegment(sketch, "E48.0.5.0", {"start": v(-88.88, -162.5) * mm, "end": v(-88.88, -171.5) * mm});
            skLineSegment(sketch, "E48.0.5.1", {"start": v(-88.88, -162.5) * mm, "end": v(-92.88, -162.5) * mm});
            skLineSegment(sketch, "E48.0.5.2", {"start": v(-92.88, -162.5) * mm, "end": v(-92.88, -171.5) * mm});
            skLineSegment(sketch, "E48.0.6.0", {"start": v(-88.88, -192.5) * mm, "end": v(-88.88, -201.5) * mm});
            skLineSegment(sketch, "E48.0.6.1", {"start": v(-88.88, -192.5) * mm, "end": v(-92.88, -192.5) * mm});
            skLineSegment(sketch, "E48.0.6.2", {"start": v(-92.88, -192.5) * mm, "end": v(-92.88, -201.5) * mm});
            skLineSegment(sketch, "E48.0.7.0", {"start": v(-88.88, -222.5) * mm, "end": v(-88.88, -231.5) * mm});
            skLineSegment(sketch, "E48.0.7.1", {"start": v(-88.88, -222.5) * mm, "end": v(-92.88, -222.5) * mm});
            skLineSegment(sketch, "E48.0.7.2", {"start": v(-92.88, -222.5) * mm, "end": v(-92.88, -231.5) * mm});
            skLineSegment(sketch, "E48.0.8.0", {"start": v(-88.88, -252.5) * mm, "end": v(-88.88, -261.5) * mm});
            skLineSegment(sketch, "E48.0.8.1", {"start": v(-88.88, -252.5) * mm, "end": v(-92.88, -252.5) * mm});
            skLineSegment(sketch, "E48.0.8.2", {"start": v(-92.88, -252.5) * mm, "end": v(-92.88, -261.5) * mm});
            skLineSegment(sketch, "E48.0.9.0", {"start": v(-88.88, -282.5) * mm, "end": v(-88.88, -291.5) * mm});
            skLineSegment(sketch, "E48.0.9.1", {"start": v(-88.88, -282.5) * mm, "end": v(-92.88, -282.5) * mm});
            skLineSegment(sketch, "E48.0.9.2", {"start": v(-92.88, -282.5) * mm, "end": v(-92.88, -291.5) * mm});
            skLineSegment(sketch, "E48.direction1", {"start": v(-88.88, -21.5) * mm, "end": v(-63.88, -21.5) * mm, "construction": true});
            skLineSegment(sketch, "E48.direction2", {"start": v(-88.88, -21.5) * mm, "end": v(-88.88, -51.5) * mm, "construction": true});
            skLineSegment(sketch, "E49.0.1.0", {"start": v(-88.88, -51.5) * mm, "end": v(-92.88, -51.5) * mm});
            skLineSegment(sketch, "E49.0.2.0", {"start": v(-88.88, -81.5) * mm, "end": v(-92.88, -81.5) * mm});
            skLineSegment(sketch, "E49.0.3.0", {"start": v(-88.88, -111.5) * mm, "end": v(-92.88, -111.5) * mm});
            skLineSegment(sketch, "E49.0.4.0", {"start": v(-88.88, -141.5) * mm, "end": v(-92.88, -141.5) * mm});
            skLineSegment(sketch, "E49.0.5.0", {"start": v(-88.88, -171.5) * mm, "end": v(-92.88, -171.5) * mm});
            skLineSegment(sketch, "E49.0.6.0", {"start": v(-88.88, -201.5) * mm, "end": v(-92.88, -201.5) * mm});
            skLineSegment(sketch, "E49.0.7.0", {"start": v(-88.88, -231.5) * mm, "end": v(-92.88, -231.5) * mm});
            skLineSegment(sketch, "E49.0.8.0", {"start": v(-88.88, -261.5) * mm, "end": v(-92.88, -261.5) * mm});
            skLineSegment(sketch, "E49.0.9.0", {"start": v(-88.88, -291.5) * mm, "end": v(-92.88, -291.5) * mm});
            skLineSegment(sketch, "E49.direction1", {"start": v(-92.88, -21.5) * mm, "end": v(-67.88, -21.5) * mm, "construction": true});
            skLineSegment(sketch, "E49.direction2", {"start": v(-92.88, -21.5) * mm, "end": v(-92.88, -51.5) * mm, "construction": true});
            skPoint(sketch, "E50.startSnap0", {"position": v(1.12, -296) * mm});
            skPoint(sketch, "E50.endSnap0", {"position": v(1.12, -296) * mm});
            skLineSegment(sketch, "E51", {"start": v(1.12, -296) * mm, "end": v(1.12, -4) * mm, "construction": true});
            skLineSegment(sketch, "E52.MirrorCS", {"start": v(91.12, -282.5) * mm, "end": v(91.12, -291.5) * mm});
            skLineSegment(sketch, "E53.MirrorCS", {"start": v(91.12, -291.5) * mm, "end": v(95.12, -291.5) * mm});
            skLineSegment(sketch, "E54.MirrorCS", {"start": v(95.12, -282.5) * mm, "end": v(95.12, -291.5) * mm});
            skLineSegment(sketch, "E55.MirrorCS", {"start": v(91.12, -282.5) * mm, "end": v(95.12, -282.5) * mm});
            skLineSegment(sketch, "E56.0.1.0", {"start": v(91.12, -252.5) * mm, "end": v(95.12, -252.5) * mm});
            skLineSegment(sketch, "E56.0.1.1", {"start": v(91.12, -252.5) * mm, "end": v(91.12, -261.5) * mm});
            skLineSegment(sketch, "E56.0.1.2", {"start": v(91.12, -261.5) * mm, "end": v(95.12, -261.5) * mm});
            skLineSegment(sketch, "E56.0.1.3", {"start": v(95.12, -252.5) * mm, "end": v(95.12, -261.5) * mm});
            skLineSegment(sketch, "E56.0.2.0", {"start": v(91.12, -222.5) * mm, "end": v(95.12, -222.5) * mm});
            skLineSegment(sketch, "E56.0.2.1", {"start": v(91.12, -222.5) * mm, "end": v(91.12, -231.5) * mm});
            skLineSegment(sketch, "E56.0.2.2", {"start": v(91.12, -231.5) * mm, "end": v(95.12, -231.5) * mm});
            skLineSegment(sketch, "E56.0.2.3", {"start": v(95.12, -222.5) * mm, "end": v(95.12, -231.5) * mm});
            skLineSegment(sketch, "E56.0.3.0", {"start": v(91.12, -192.5) * mm, "end": v(95.12, -192.5) * mm});
            skLineSegment(sketch, "E56.0.3.1", {"start": v(91.12, -192.5) * mm, "end": v(91.12, -201.5) * mm});
            skLineSegment(sketch, "E56.0.3.2", {"start": v(91.12, -201.5) * mm, "end": v(95.12, -201.5) * mm});
            skLineSegment(sketch, "E56.0.3.3", {"start": v(95.12, -192.5) * mm, "end": v(95.12, -201.5) * mm});
            skLineSegment(sketch, "E56.0.4.0", {"start": v(91.12, -162.5) * mm, "end": v(95.12, -162.5) * mm});
            skLineSegment(sketch, "E56.0.4.1", {"start": v(91.12, -162.5) * mm, "end": v(91.12, -171.5) * mm});
            skLineSegment(sketch, "E56.0.4.2", {"start": v(91.12, -171.5) * mm, "end": v(95.12, -171.5) * mm});
            skLineSegment(sketch, "E56.0.4.3", {"start": v(95.12, -162.5) * mm, "end": v(95.12, -171.5) * mm});
            skLineSegment(sketch, "E56.0.5.0", {"start": v(91.12, -132.5) * mm, "end": v(95.12, -132.5) * mm});
            skLineSegment(sketch, "E56.0.5.1", {"start": v(91.12, -132.5) * mm, "end": v(91.12, -141.5) * mm});
            skLineSegment(sketch, "E56.0.5.2", {"start": v(91.12, -141.5) * mm, "end": v(95.12, -141.5) * mm});
            skLineSegment(sketch, "E56.0.5.3", {"start": v(95.12, -132.5) * mm, "end": v(95.12, -141.5) * mm});
            skLineSegment(sketch, "E56.0.6.0", {"start": v(91.12, -102.5) * mm, "end": v(95.12, -102.5) * mm});
            skLineSegment(sketch, "E56.0.6.1", {"start": v(91.12, -102.5) * mm, "end": v(91.12, -111.5) * mm});
            skLineSegment(sketch, "E56.0.6.2", {"start": v(91.12, -111.5) * mm, "end": v(95.12, -111.5) * mm});
            skLineSegment(sketch, "E56.0.6.3", {"start": v(95.12, -102.5) * mm, "end": v(95.12, -111.5) * mm});
            skLineSegment(sketch, "E56.0.7.0", {"start": v(91.12, -72.5) * mm, "end": v(95.12, -72.5) * mm});
            skLineSegment(sketch, "E56.0.7.1", {"start": v(91.12, -72.5) * mm, "end": v(91.12, -81.5) * mm});
            skLineSegment(sketch, "E56.0.7.2", {"start": v(91.12, -81.5) * mm, "end": v(95.12, -81.5) * mm});
            skLineSegment(sketch, "E56.0.7.3", {"start": v(95.12, -72.5) * mm, "end": v(95.12, -81.5) * mm});
            skLineSegment(sketch, "E56.0.8.0", {"start": v(91.12, -42.5) * mm, "end": v(95.12, -42.5) * mm});
            skLineSegment(sketch, "E56.0.8.1", {"start": v(91.12, -42.5) * mm, "end": v(91.12, -51.5) * mm});
            skLineSegment(sketch, "E56.0.8.2", {"start": v(91.12, -51.5) * mm, "end": v(95.12, -51.5) * mm});
            skLineSegment(sketch, "E56.0.8.3", {"start": v(95.12, -42.5) * mm, "end": v(95.12, -51.5) * mm});
            skLineSegment(sketch, "E56.0.9.0", {"start": v(91.12, -12.5) * mm, "end": v(95.12, -12.5) * mm});
            skLineSegment(sketch, "E56.0.9.1", {"start": v(91.12, -12.5) * mm, "end": v(91.12, -21.5) * mm});
            skLineSegment(sketch, "E56.0.9.2", {"start": v(91.12, -21.5) * mm, "end": v(95.12, -21.5) * mm});
            skLineSegment(sketch, "E56.0.9.3", {"start": v(95.12, -12.5) * mm, "end": v(95.12, -21.5) * mm});
            skLineSegment(sketch, "E56.direction1", {"start": v(91.12, -282.5) * mm, "end": v(116.12, -282.5) * mm, "construction": true});
            skLineSegment(sketch, "E56.direction2", {"start": v(91.12, -282.5) * mm, "end": v(91.12, -252.5) * mm, "construction": true});
            skSolve(sketch);
        }
        {
            var Q0;
            Q0=makeQuery(id+"F13.imprint","IMPRINT",FACE,{"disambiguationData":[TD([[makeQuery(id+"F13.imprint","IMPRINT",EDGE,{"derivedFrom":sQuery(id+"F13.wireOp",EDGE,"E47.bottom")}),1.0]])]});
            var Q1;
            Q1=makeQuery(id+"F13.imprint","IMPRINT",FACE,{"disambiguationData":[TD([[makeQuery(id+"F13.imprint","IMPRINT",EDGE,{"derivedFrom":sQuery(id+"F13.wireOp",EDGE,"E48.0.1.0")}),-1.0]])]});
            var Q2;
            Q2=makeQuery(id+"F13.imprint","IMPRINT",FACE,{"disambiguationData":[TD([[makeQuery(id+"F13.imprint","IMPRINT",EDGE,{"derivedFrom":sQuery(id+"F13.wireOp",EDGE,"E48.0.2.0")}),-1.0]])]});
            var Q3;
            Q3=makeQuery(id+"F13.imprint","IMPRINT",FACE,{"disambiguationData":[TD([[makeQuery(id+"F13.imprint","IMPRINT",EDGE,{"derivedFrom":sQuery(id+"F13.wireOp",EDGE,"E48.0.3.0")}),-1.0]])]});
            var Q4;
            Q4=makeQuery(id+"F13.imprint","IMPRINT",FACE,{"disambiguationData":[TD([[makeQuery(id+"F13.imprint","IMPRINT",EDGE,{"derivedFrom":sQuery(id+"F13.wireOp",EDGE,"E48.0.4.0")}),-1.0]])]});
            var Q5;
            Q5=makeQuery(id+"F13.imprint","IMPRINT",FACE,{"disambiguationData":[TD([[makeQuery(id+"F13.imprint","IMPRINT",EDGE,{"derivedFrom":sQuery(id+"F13.wireOp",EDGE,"E48.0.5.0")}),-1.0]])]});
            var Q6;
            Q6=makeQuery(id+"F13.imprint","IMPRINT",FACE,{"disambiguationData":[TD([[makeQuery(id+"F13.imprint","IMPRINT",EDGE,{"derivedFrom":sQuery(id+"F13.wireOp",EDGE,"E48.0.6.0")}),-1.0]])]});
            var Q7;
            Q7=makeQuery(id+"F13.imprint","IMPRINT",FACE,{"disambiguationData":[TD([[makeQuery(id+"F13.imprint","IMPRINT",EDGE,{"derivedFrom":sQuery(id+"F13.wireOp",EDGE,"E48.0.7.0")}),-1.0]])]});
            var Q8;
            Q8=makeQuery(id+"F13.imprint","IMPRINT",FACE,{"disambiguationData":[TD([[makeQuery(id+"F13.imprint","IMPRINT",EDGE,{"derivedFrom":sQuery(id+"F13.wireOp",EDGE,"E48.0.8.0")}),-1.0]])]});
            var Q9;
            Q9=makeQuery(id+"F13.imprint","IMPRINT",FACE,{"disambiguationData":[TD([[makeQuery(id+"F13.imprint","IMPRINT",EDGE,{"derivedFrom":sQuery(id+"F13.wireOp",EDGE,"E48.0.9.0")}),-1.0]])]});
            var Q10;
            Q10=makeQuery(id+"F13.imprint","IMPRINT",FACE,{"disambiguationData":[TD([[makeQuery(id+"F13.imprint","IMPRINT",EDGE,{"derivedFrom":sQuery(id+"F13.wireOp",EDGE,"E52.MirrorCS")}),1.0]])]});
            var Q11;
            Q11=makeQuery(id+"F13.imprint","IMPRINT",FACE,{"disambiguationData":[TD([[makeQuery(id+"F13.imprint","IMPRINT",EDGE,{"derivedFrom":sQuery(id+"F13.wireOp",EDGE,"E56.0.1.0")}),-1.0]])]});
            var Q12;
            Q12=makeQuery(id+"F13.imprint","IMPRINT",FACE,{"disambiguationData":[TD([[makeQuery(id+"F13.imprint","IMPRINT",EDGE,{"derivedFrom":sQuery(id+"F13.wireOp",EDGE,"E56.0.2.0")}),-1.0]])]});
            var Q13;
            Q13=makeQuery(id+"F13.imprint","IMPRINT",FACE,{"disambiguationData":[TD([[makeQuery(id+"F13.imprint","IMPRINT",EDGE,{"derivedFrom":sQuery(id+"F13.wireOp",EDGE,"E56.0.3.0")}),-1.0]])]});
            var Q14;
            Q14=makeQuery(id+"F13.imprint","IMPRINT",FACE,{"disambiguationData":[TD([[makeQuery(id+"F13.imprint","IMPRINT",EDGE,{"derivedFrom":sQuery(id+"F13.wireOp",EDGE,"E56.0.4.0")}),-1.0]])]});
            var Q15;
            Q15=makeQuery(id+"F13.imprint","IMPRINT",FACE,{"disambiguationData":[TD([[makeQuery(id+"F13.imprint","IMPRINT",EDGE,{"derivedFrom":sQuery(id+"F13.wireOp",EDGE,"E56.0.5.0")}),-1.0]])]});
            var Q16;
            Q16=makeQuery(id+"F13.imprint","IMPRINT",FACE,{"disambiguationData":[TD([[makeQuery(id+"F13.imprint","IMPRINT",EDGE,{"derivedFrom":sQuery(id+"F13.wireOp",EDGE,"E56.0.6.0")}),-1.0]])]});
            var Q17;
            Q17=makeQuery(id+"F13.imprint","IMPRINT",FACE,{"disambiguationData":[TD([[makeQuery(id+"F13.imprint","IMPRINT",EDGE,{"derivedFrom":sQuery(id+"F13.wireOp",EDGE,"E56.0.7.0")}),-1.0]])]});
            var Q18;
            Q18=makeQuery(id+"F13.imprint","IMPRINT",FACE,{"disambiguationData":[TD([[makeQuery(id+"F13.imprint","IMPRINT",EDGE,{"derivedFrom":sQuery(id+"F13.wireOp",EDGE,"E56.0.8.0")}),-1.0]])]});
            var Q19;
            Q19=makeQuery(id+"F13.imprint","IMPRINT",FACE,{"disambiguationData":[TD([[makeQuery(id+"F13.imprint","IMPRINT",EDGE,{"derivedFrom":sQuery(id+"F13.wireOp",EDGE,"E56.0.9.0")}),-1.0]])]});
            extrude(context, id + "F14", {"entities" : qUnion([Q0, Q1, Q2, Q3, Q4, Q5, Q6, Q7, Q8, Q9, Q10, Q11, Q12, Q13, Q14, Q15, Q16, Q17, Q18, Q19]), "operationType" : NewBodyOperationType.REMOVE, "oppositeDirection" : true, "depth" : 4 * mm});
        }
        {
            var Q0;
            {var subQ32=sQuery(id+"F12.wireOp",EDGE,"E29.top");Q0=makeQuery(id+"F12.imprint","IMPRINT",FACE,{"disambiguationData":[TD([[makeQuery(id+"F12.imprint","IMPRINT",EDGE,{"derivedFrom":subQ32}),-1.0]])]});}
            var sketch = newSketch(context, id + "F15", { "sketchPlane" : qUnion([Q0])});
            skLineSegment(sketch, "E57.bottom", {"start": v(-92.88, -6.77) * mm, "end": v(-88.88, -6.77) * mm});
            skLineSegment(sketch, "E57.top", {"start": v(-92.88, -81.77) * mm, "end": v(-88.88, -81.77) * mm});
            skLineSegment(sketch, "E57.left", {"start": v(-92.88, -6.77) * mm, "end": v(-92.88, -81.77) * mm});
            skLineSegment(sketch, "E57.right", {"start": v(-88.88, -6.77) * mm, "end": v(-88.88, -81.77) * mm});
            skLineSegment(sketch, "E58.top", {"start": v(-92.88, -15.77) * mm, "end": v(-88.88, -15.77) * mm});
            skLineSegment(sketch, "E58.left", {"start": v(-92.88, -6.77) * mm, "end": v(-92.88, -15.77) * mm});
            skLineSegment(sketch, "E58.right", {"start": v(-88.88, -6.77) * mm, "end": v(-88.88, -15.77) * mm});
            skLineSegment(sketch, "E59.0.1.0", {"start": v(-92.88, -17.77) * mm, "end": v(-88.88, -17.77) * mm});
            skLineSegment(sketch, "E59.0.1.1", {"start": v(-92.88, -17.77) * mm, "end": v(-92.88, -26.77) * mm});
            skLineSegment(sketch, "E59.0.1.2", {"start": v(-92.88, -26.77) * mm, "end": v(-88.88, -26.77) * mm});
            skLineSegment(sketch, "E59.0.1.3", {"start": v(-88.88, -17.77) * mm, "end": v(-88.88, -26.77) * mm});
            skLineSegment(sketch, "E59.0.2.0", {"start": v(-92.88, -28.77) * mm, "end": v(-88.88, -28.77) * mm});
            skLineSegment(sketch, "E59.0.2.1", {"start": v(-92.88, -28.77) * mm, "end": v(-92.88, -37.77) * mm});
            skLineSegment(sketch, "E59.0.2.2", {"start": v(-92.88, -37.77) * mm, "end": v(-88.88, -37.77) * mm});
            skLineSegment(sketch, "E59.0.2.3", {"start": v(-88.88, -28.77) * mm, "end": v(-88.88, -37.77) * mm});
            skLineSegment(sketch, "E59.0.3.0", {"start": v(-92.88, -39.77) * mm, "end": v(-88.88, -39.77) * mm});
            skLineSegment(sketch, "E59.0.3.1", {"start": v(-92.88, -39.77) * mm, "end": v(-92.88, -48.77) * mm});
            skLineSegment(sketch, "E59.0.3.2", {"start": v(-92.88, -48.77) * mm, "end": v(-88.88, -48.77) * mm});
            skLineSegment(sketch, "E59.0.3.3", {"start": v(-88.88, -39.77) * mm, "end": v(-88.88, -48.77) * mm});
            skLineSegment(sketch, "E59.0.4.0", {"start": v(-92.88, -50.77) * mm, "end": v(-88.88, -50.77) * mm});
            skLineSegment(sketch, "E59.0.4.1", {"start": v(-92.88, -50.77) * mm, "end": v(-92.88, -59.77) * mm});
            skLineSegment(sketch, "E59.0.4.2", {"start": v(-92.88, -59.77) * mm, "end": v(-88.88, -59.77) * mm});
            skLineSegment(sketch, "E59.0.4.3", {"start": v(-88.88, -50.77) * mm, "end": v(-88.88, -59.77) * mm});
            skLineSegment(sketch, "E59.0.5.0", {"start": v(-92.88, -61.77) * mm, "end": v(-88.88, -61.77) * mm});
            skLineSegment(sketch, "E59.0.5.1", {"start": v(-92.88, -61.77) * mm, "end": v(-92.88, -70.77) * mm});
            skLineSegment(sketch, "E59.0.5.2", {"start": v(-92.88, -70.77) * mm, "end": v(-88.88, -70.77) * mm});
            skLineSegment(sketch, "E59.0.5.3", {"start": v(-88.88, -61.77) * mm, "end": v(-88.88, -70.77) * mm});
            skLineSegment(sketch, "E59.0.6.0", {"start": v(-92.88, -72.77) * mm, "end": v(-88.88, -72.77) * mm});
            skLineSegment(sketch, "E59.0.6.1", {"start": v(-92.88, -72.77) * mm, "end": v(-92.88, -81.77) * mm});
            skLineSegment(sketch, "E59.0.6.3", {"start": v(-88.88, -72.77) * mm, "end": v(-88.88, -81.77) * mm});
            skLineSegment(sketch, "E59.direction1", {"start": v(-92.88, -6.77) * mm, "end": v(-67.88, -6.77) * mm, "construction": true});
            skLineSegment(sketch, "E59.direction2", {"start": v(-92.88, -6.77) * mm, "end": v(-92.88, -17.77) * mm, "construction": true});
            skLineSegment(sketch, "E60.MirrorCS", {"start": v(91.12, -6.77) * mm, "end": v(91.12, -15.77) * mm});
            skLineSegment(sketch, "E61.MirrorCS", {"start": v(95.12, -6.77) * mm, "end": v(95.12, -81.77) * mm});
            skLineSegment(sketch, "E62.MirrorCS", {"start": v(91.12, -6.77) * mm, "end": v(91.12, -81.77) * mm});
            skLineSegment(sketch, "E63.MirrorCS", {"start": v(95.12, -28.77) * mm, "end": v(91.12, -28.77) * mm});
            skLineSegment(sketch, "E64.MirrorCS", {"start": v(95.12, -26.77) * mm, "end": v(91.12, -26.77) * mm});
            skLineSegment(sketch, "E65.MirrorCS", {"start": v(95.12, -17.77) * mm, "end": v(91.12, -17.77) * mm});
            skLineSegment(sketch, "E66.MirrorCS", {"start": v(95.12, -15.77) * mm, "end": v(91.12, -15.77) * mm});
            skLineSegment(sketch, "E67.MirrorCS", {"start": v(95.12, -39.77) * mm, "end": v(91.12, -39.77) * mm});
            skLineSegment(sketch, "E68.MirrorCS", {"start": v(95.12, -48.77) * mm, "end": v(91.12, -48.77) * mm});
            skLineSegment(sketch, "E69.MirrorCS", {"start": v(95.12, -50.77) * mm, "end": v(91.12, -50.77) * mm});
            skLineSegment(sketch, "E70.MirrorCS", {"start": v(95.12, -59.77) * mm, "end": v(91.12, -59.77) * mm});
            skLineSegment(sketch, "E71.MirrorCS", {"start": v(95.12, -61.77) * mm, "end": v(91.12, -61.77) * mm});
            skLineSegment(sketch, "E72.MirrorCS", {"start": v(95.12, -70.77) * mm, "end": v(91.12, -70.77) * mm});
            skLineSegment(sketch, "E73.MirrorCS", {"start": v(95.12, -72.77) * mm, "end": v(91.12, -72.77) * mm});
            skLineSegment(sketch, "E74.MirrorCS", {"start": v(95.12, -37.77) * mm, "end": v(91.12, -37.77) * mm});
            skLineSegment(sketch, "E75.MirrorCS", {"start": v(95.12, -6.77) * mm, "end": v(70.12, -6.77) * mm, "construction": true});
            skLineSegment(sketch, "E76", {"start": v(91.12, -6.77) * mm, "end": v(95.12, -6.77) * mm});
            skLineSegment(sketch, "E77.bottom", {"start": v(91.12, -81.77) * mm, "end": v(95.12, -81.77) * mm});
            skLineSegment(sketch, "E77.top", {"start": v(91.12, -84.77) * mm, "end": v(95.12, -84.77) * mm});
            skLineSegment(sketch, "E77.left", {"start": v(91.12, -81.77) * mm, "end": v(91.12, -84.77) * mm});
            skLineSegment(sketch, "E77.right", {"start": v(95.12, -81.77) * mm, "end": v(95.12, -84.77) * mm});
            skSolve(sketch);
        }
        {
            var Q0;
            Q0=makeQuery(id+"F0.imprint","IMPRINT",FACE,{"disambiguationData":[TD([[makeQuery(id+"F0.imprint","IMPRINT",EDGE,{"derivedFrom":sQuery(id+"F0.wireOp",EDGE,"E12.0.6.0")}),1.0]])]});
            var Q1;
            Q1=makeQuery(id+"F0.imprint","IMPRINT",FACE,{"disambiguationData":[TD([[makeQuery(id+"F0.imprint","IMPRINT",EDGE,{"derivedFrom":sQuery(id+"F0.wireOp",EDGE,"E12.0.5.0")}),1.0]])]});
            var Q2;
            Q2=makeQuery(id+"F0.imprint","IMPRINT",FACE,{"disambiguationData":[TD([[makeQuery(id+"F0.imprint","IMPRINT",EDGE,{"derivedFrom":sQuery(id+"F0.wireOp",EDGE,"E12.0.4.0")}),1.0]])]});
            var Q3;
            Q3=makeQuery(id+"F0.imprint","IMPRINT",FACE,{"disambiguationData":[TD([[makeQuery(id+"F0.imprint","IMPRINT",EDGE,{"derivedFrom":sQuery(id+"F0.wireOp",EDGE,"E12.0.3.0")}),1.0]])]});
            var Q4;
            Q4=makeQuery(id+"F0.imprint","IMPRINT",FACE,{"disambiguationData":[TD([[makeQuery(id+"F0.imprint","IMPRINT",EDGE,{"derivedFrom":sQuery(id+"F0.wireOp",EDGE,"E12.0.2.0")}),1.0]])]});
            var Q5;
            Q5=makeQuery(id+"F0.imprint","IMPRINT",FACE,{"disambiguationData":[TD([[makeQuery(id+"F0.imprint","IMPRINT",EDGE,{"derivedFrom":sQuery(id+"F0.wireOp",EDGE,"E12.0.1.0")}),1.0]])]});
            var Q6;
            Q6=makeQuery(id+"F0.imprint","IMPRINT",FACE,{"disambiguationData":[TD([[makeQuery(id+"F0.imprint","IMPRINT",EDGE,{"derivedFrom":sQuery(id+"F0.wireOp",EDGE,"E11.bottom")}),-1.0]])]});
            var Q7;
            Q7=makeQuery(id+"F0.imprint","IMPRINT",FACE,{"disambiguationData":[TD([[makeQuery(id+"F0.imprint","IMPRINT",EDGE,{"derivedFrom":sQuery(id+"F0.wireOp",EDGE,"E19.0.6.0")}),-1.0]])]});
            var Q8;
            Q8=makeQuery(id+"F0.imprint","IMPRINT",FACE,{"disambiguationData":[TD([[makeQuery(id+"F0.imprint","IMPRINT",EDGE,{"derivedFrom":sQuery(id+"F0.wireOp",EDGE,"E19.0.5.0")}),-1.0]])]});
            var Q9;
            Q9=makeQuery(id+"F0.imprint","IMPRINT",FACE,{"disambiguationData":[TD([[makeQuery(id+"F0.imprint","IMPRINT",EDGE,{"derivedFrom":sQuery(id+"F0.wireOp",EDGE,"E19.0.4.0")}),-1.0]])]});
            var Q10;
            Q10=makeQuery(id+"F0.imprint","IMPRINT",FACE,{"disambiguationData":[TD([[makeQuery(id+"F0.imprint","IMPRINT",EDGE,{"derivedFrom":sQuery(id+"F0.wireOp",EDGE,"E19.0.3.0")}),-1.0]])]});
            var Q11;
            Q11=makeQuery(id+"F0.imprint","IMPRINT",FACE,{"disambiguationData":[TD([[makeQuery(id+"F0.imprint","IMPRINT",EDGE,{"derivedFrom":sQuery(id+"F0.wireOp",EDGE,"E19.0.2.0")}),-1.0]])]});
            var Q12;
            Q12=makeQuery(id+"F0.imprint","IMPRINT",FACE,{"disambiguationData":[TD([[makeQuery(id+"F0.imprint","IMPRINT",EDGE,{"derivedFrom":sQuery(id+"F0.wireOp",EDGE,"E19.0.1.0")}),-1.0]])]});
            var Q13;
            Q13=makeQuery(id+"F0.imprint","IMPRINT",FACE,{"disambiguationData":[TD([[makeQuery(id+"F0.imprint","IMPRINT",EDGE,{"derivedFrom":sQuery(id+"F0.wireOp",EDGE,"E14.MirrorCS")}),1.0]])]});
            extrude(context, id + "F16", {"entities" : qUnion([Q0, Q1, Q2, Q3, Q4, Q5, Q6, Q7, Q8, Q9, Q10, Q11, Q12, Q13]), "depth" : 300 * mm});
        }
        {
            var Q0;
            {var subQ0=sQuery(id+"F12.wireOp",EDGE,"E29.bottom");Q0=makeQuery(id+"F12.imprint","IMPRINT",FACE,{"disambiguationData":[TD([[makeQuery(id+"F12.imprint","IMPRINT",EDGE,{"derivedFrom":subQ0}),-1.0]])]});}
            var Q1;
            {var subQ2=sQuery(id+"F12.wireOp",EDGE,"E32.top");Q1=makeQuery(id+"F12.imprint","IMPRINT",FACE,{"disambiguationData":[TD([[makeQuery(id+"F12.imprint","IMPRINT",EDGE,{"derivedFrom":subQ2}),1.0]])]});}
            var Q2;
            {var subQ2=sQuery(id+"F12.wireOp",EDGE,"E34.0.1.3");Q2=makeQuery(id+"F12.imprint","IMPRINT",FACE,{"disambiguationData":[TD([[makeQuery(id+"F12.imprint","IMPRINT",EDGE,{"derivedFrom":subQ2}),1.0]])]});}
            var Q3;
            {var subQ2=sQuery(id+"F12.wireOp",EDGE,"E34.0.2.3");Q3=makeQuery(id+"F12.imprint","IMPRINT",FACE,{"disambiguationData":[TD([[makeQuery(id+"F12.imprint","IMPRINT",EDGE,{"derivedFrom":subQ2}),1.0]])]});}
            var Q4;
            {var subQ2=sQuery(id+"F12.wireOp",EDGE,"E34.0.3.3");Q4=makeQuery(id+"F12.imprint","IMPRINT",FACE,{"disambiguationData":[TD([[makeQuery(id+"F12.imprint","IMPRINT",EDGE,{"derivedFrom":subQ2}),1.0]])]});}
            var Q5;
            {var subQ2=sQuery(id+"F12.wireOp",EDGE,"E34.0.4.3");Q5=makeQuery(id+"F12.imprint","IMPRINT",FACE,{"disambiguationData":[TD([[makeQuery(id+"F12.imprint","IMPRINT",EDGE,{"derivedFrom":subQ2}),1.0]])]});}
            var Q6;
            {var subQ2=sQuery(id+"F12.wireOp",EDGE,"E34.0.5.3");Q6=makeQuery(id+"F12.imprint","IMPRINT",FACE,{"disambiguationData":[TD([[makeQuery(id+"F12.imprint","IMPRINT",EDGE,{"derivedFrom":subQ2}),1.0]])]});}
            var Q7;
            {var subQ0=sQuery(id+"F12.wireOp",EDGE,"E29.top");Q7=makeQuery(id+"F12.imprint","IMPRINT",FACE,{"disambiguationData":[TD([[makeQuery(id+"F12.imprint","IMPRINT",EDGE,{"derivedFrom":subQ0}),1.0]])]});}
            var Q8;
            {var subQ0=sQuery(id+"F12.wireOp",EDGE,"E33.bottom");Q8=makeQuery(id+"F12.imprint","IMPRINT",FACE,{"disambiguationData":[TD([[makeQuery(id+"F12.imprint","IMPRINT",EDGE,{"derivedFrom":subQ0}),1.0]])]});}
            var Q9;
            {var subQ2=sQuery(id+"F12.wireOp",EDGE,"E33.top");Q9=makeQuery(id+"F12.imprint","IMPRINT",FACE,{"disambiguationData":[TD([[makeQuery(id+"F12.imprint","IMPRINT",EDGE,{"derivedFrom":subQ2}),-1.0]])]});}
            var Q10;
            {var subQ0=sQuery(id+"F12.wireOp",EDGE,"E36.MirrorCS");Q10=makeQuery(id+"F12.imprint","IMPRINT",FACE,{"disambiguationData":[TD([[makeQuery(id+"F12.imprint","IMPRINT",EDGE,{"derivedFrom":subQ0}),1.0]])]});}
            var Q11;
            {var subQ0=sQuery(id+"F15.wireOp",EDGE,"E67.MirrorCS");Q11=makeQuery(id+"F15.imprint","IMPRINT",FACE,{"disambiguationData":[TD([[makeQuery(id+"F15.imprint","IMPRINT",EDGE,{"derivedFrom":subQ0}),-1.0]])]});}
            var Q12;
            {var subQ2=sQuery(id+"F15.wireOp",EDGE,"E68.MirrorCS");Q12=makeQuery(id+"F15.imprint","IMPRINT",FACE,{"disambiguationData":[TD([[makeQuery(id+"F15.imprint","IMPRINT",EDGE,{"derivedFrom":subQ2}),1.0]])]});}
            var Q13;
            {var subQ2=sQuery(id+"F12.wireOp",EDGE,"E42.MirrorCS");Q13=makeQuery(id+"F12.imprint","IMPRINT",FACE,{"disambiguationData":[TD([[makeQuery(id+"F12.imprint","IMPRINT",EDGE,{"derivedFrom":subQ2}),-1.0]])]});}
            var Q14;
            {var subQ2=sQuery(id+"F12.wireOp",EDGE,"E44.MirrorCS");Q14=makeQuery(id+"F12.imprint","IMPRINT",FACE,{"disambiguationData":[TD([[makeQuery(id+"F12.imprint","IMPRINT",EDGE,{"derivedFrom":subQ2}),-1.0]])]});}
            var Q15;
            Q15=makeQuery(id+"F15.imprint","IMPRINT",FACE,{"disambiguationData":[TD([[makeQuery(id+"F15.imprint","IMPRINT",EDGE,{"derivedFrom":sQuery(id+"F15.wireOp",EDGE,"E77.bottom")}),-1.0]])]});
            extrude(context, id + "F17", {"entities" : qUnion([Q0, Q1, Q2, Q3, Q4, Q5, Q6, Q7, Q8, Q9, Q10, Q11, Q12, Q13, Q14, Q15]), "depth" : 292 * mm});
        }
        {
            var Q0;
            Q0=makeQuery(id+"F16.opExtrude","SWEPT_BODY",BODY,{"disambiguationData":[OSD([sQuery(id+"F0.wireOp",EDGE,"E14.MirrorCS"),sQuery(id+"F0.wireOp",EDGE,"E15.MirrorCS"),sQuery(id+"F0.wireOp",EDGE,"E16.MirrorCS"),sQuery(id+"F0.wireOp",EDGE,"E18.MirrorCS")])]});
            deleteBodies(context, id + "F18", {"entities" : qUnion([Q0])});
        }
        {
            var Q0;
            Q0=makeQuery(id+"F13.imprint","IMPRINT",FACE,{"disambiguationData":[TD([[makeQuery(id+"F13.imprint","IMPRINT",EDGE,{"derivedFrom":sQuery(id+"F13.wireOp",EDGE,"E47.bottom")}),1.0]])]});
            var Q1;
            Q1=makeQuery(id+"F13.imprint","IMPRINT",FACE,{"disambiguationData":[TD([[makeQuery(id+"F13.imprint","IMPRINT",EDGE,{"derivedFrom":sQuery(id+"F13.wireOp",EDGE,"E48.0.1.0")}),-1.0]])]});
            var Q2;
            Q2=makeQuery(id+"F13.imprint","IMPRINT",FACE,{"disambiguationData":[TD([[makeQuery(id+"F13.imprint","IMPRINT",EDGE,{"derivedFrom":sQuery(id+"F13.wireOp",EDGE,"E48.0.2.0")}),-1.0]])]});
            var Q3;
            Q3=makeQuery(id+"F13.imprint","IMPRINT",FACE,{"disambiguationData":[TD([[makeQuery(id+"F13.imprint","IMPRINT",EDGE,{"derivedFrom":sQuery(id+"F13.wireOp",EDGE,"E48.0.3.0")}),-1.0]])]});
            var Q4;
            Q4=makeQuery(id+"F13.imprint","IMPRINT",FACE,{"disambiguationData":[TD([[makeQuery(id+"F13.imprint","IMPRINT",EDGE,{"derivedFrom":sQuery(id+"F13.wireOp",EDGE,"E48.0.5.0")}),-1.0]])]});
            var Q5;
            Q5=makeQuery(id+"F13.imprint","IMPRINT",FACE,{"disambiguationData":[TD([[makeQuery(id+"F13.imprint","IMPRINT",EDGE,{"derivedFrom":sQuery(id+"F13.wireOp",EDGE,"E48.0.7.0")}),-1.0]])]});
            var Q6;
            Q6=makeQuery(id+"F13.imprint","IMPRINT",FACE,{"disambiguationData":[TD([[makeQuery(id+"F13.imprint","IMPRINT",EDGE,{"derivedFrom":sQuery(id+"F13.wireOp",EDGE,"E48.0.8.0")}),-1.0]])]});
            var Q7;
            Q7=makeQuery(id+"F13.imprint","IMPRINT",FACE,{"disambiguationData":[TD([[makeQuery(id+"F13.imprint","IMPRINT",EDGE,{"derivedFrom":sQuery(id+"F13.wireOp",EDGE,"E48.0.9.0")}),-1.0]])]});
            var Q8;
            Q8=makeQuery(id+"F13.imprint","IMPRINT",FACE,{"disambiguationData":[TD([[makeQuery(id+"F13.imprint","IMPRINT",EDGE,{"derivedFrom":sQuery(id+"F13.wireOp",EDGE,"E48.0.6.0")}),-1.0]])]});
            var Q9;
            Q9=makeQuery(id+"F13.imprint","IMPRINT",FACE,{"disambiguationData":[TD([[makeQuery(id+"F13.imprint","IMPRINT",EDGE,{"derivedFrom":sQuery(id+"F13.wireOp",EDGE,"E48.0.4.0")}),-1.0]])]});
            extrude(context, id + "F19", {"entities" : qUnion([Q0, Q1, Q2, Q3, Q4, Q5, Q6, Q7, Q8, Q9]), "oppositeDirection" : true, "depth" : 4 * mm});
        }
    });
